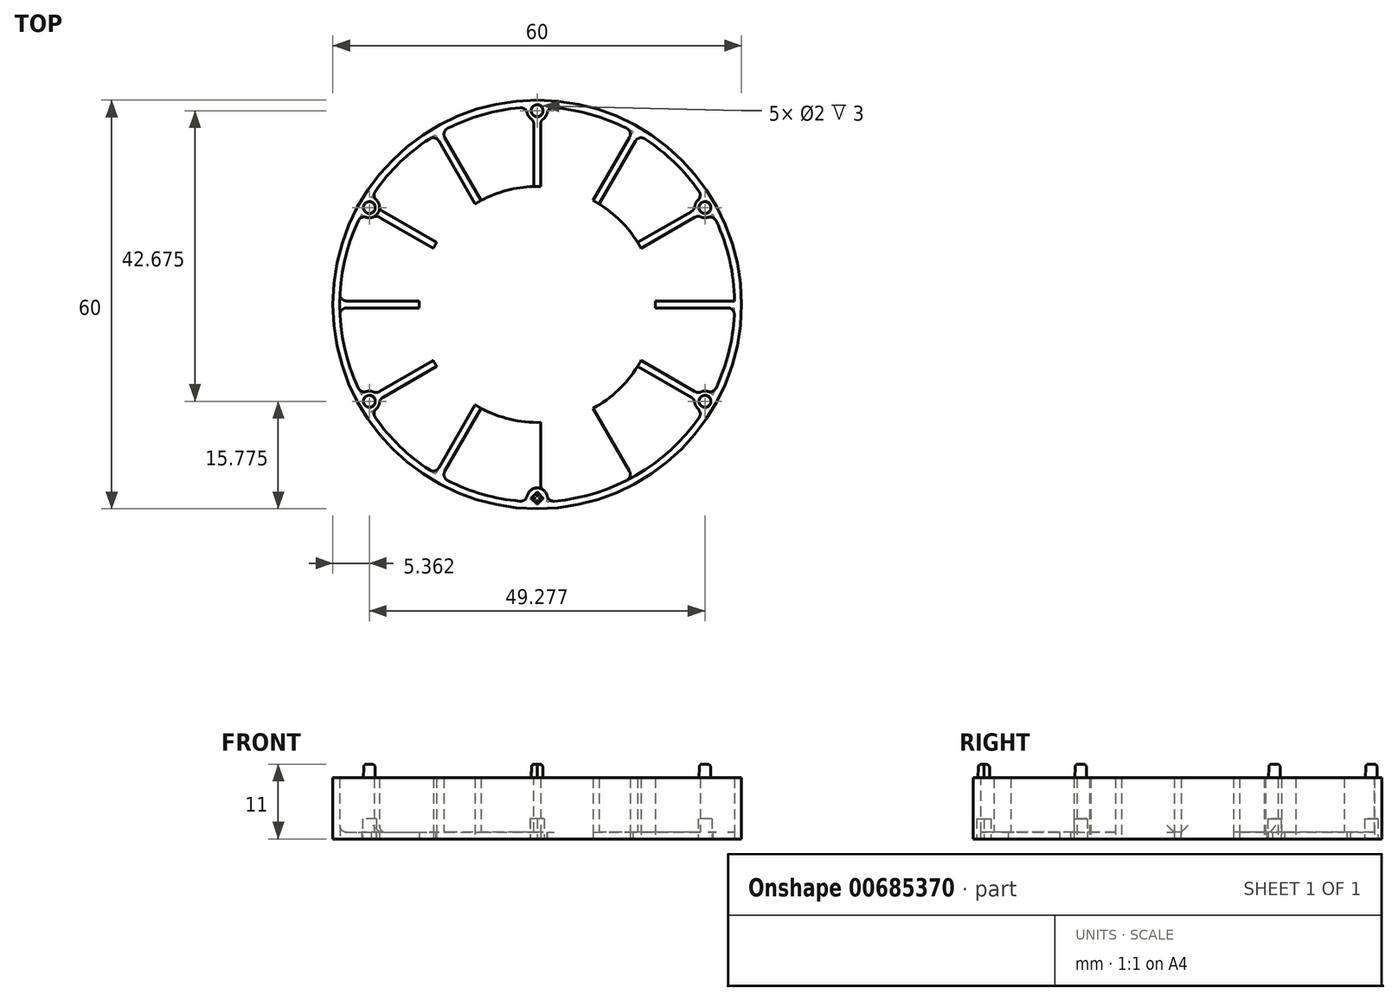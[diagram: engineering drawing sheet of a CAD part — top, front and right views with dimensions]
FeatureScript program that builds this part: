
annotation { "Feature Type Name" : "Feature", "Feature Type Description" : "" }
export const myFeature = defineFeature(function(context is Context, id is Id, definition is map)
    precondition{}
    {
        {
            var Q0;
            Q0=qCreatedBy(makeId("Top.planeOp"),FACE);
            var sketch = newSketch(context, id + "F0", { "sketchPlane" : qUnion([Q0])});
            skCircle(sketch, "E0", {"center": v(0, 0) * mm, "radius": 30 * mm});
            skCircle(sketch, "E1.0", {"center": v(0, 0) * mm, "radius": 29 * mm});
            skLineSegment(sketch, "E2.bottom", {"start": v(14.56, 26.23) * mm, "end": v(15.43, 25.73) * mm});
            skLineSegment(sketch, "E2.top", {"start": v(-15.43, -25.73) * mm, "end": v(-14.56, -26.23) * mm});
            skLineSegment(sketch, "E2.left", {"start": v(14.56, 26.23) * mm, "end": v(-15.43, -25.73) * mm});
            skLineSegment(sketch, "E2.right", {"start": v(15.43, 25.73) * mm, "end": v(-14.56, -26.23) * mm});
            skLineSegment(sketch, "E3.bottom", {"start": v(25.73, 15.43) * mm, "end": v(26.23, 14.56) * mm});
            skLineSegment(sketch, "E3.top", {"start": v(-26.23, -14.56) * mm, "end": v(-25.73, -15.43) * mm});
            skLineSegment(sketch, "E3.left", {"start": v(25.73, 15.43) * mm, "end": v(-26.23, -14.56) * mm});
            skLineSegment(sketch, "E3.right", {"start": v(26.23, 14.56) * mm, "end": v(-25.73, -15.43) * mm});
            skLineSegment(sketch, "E4", {"start": v(-38.35, 0) * mm, "end": v(39.17, 0) * mm, "construction": true});
            skLineSegment(sketch, "E5", {"start": v(0, 42.5) * mm, "end": v(0, -42.47) * mm, "construction": true});
            skLineSegment(sketch, "E6.bottom", {"start": v(-30, 0.5) * mm, "end": v(30, 0.5) * mm});
            skLineSegment(sketch, "E6.top", {"start": v(-30, -0.5) * mm, "end": v(30, -0.5) * mm});
            skLineSegment(sketch, "E6.left", {"start": v(-30, 0.5) * mm, "end": v(-30, -0.5) * mm});
            skLineSegment(sketch, "E6.right", {"start": v(30, 0.5) * mm, "end": v(30, -0.5) * mm});
            skLineSegment(sketch, "E7.bottom", {"start": v(-25.73, 15.43) * mm, "end": v(26.23, -14.56) * mm});
            skLineSegment(sketch, "E7.top", {"start": v(-26.23, 14.56) * mm, "end": v(25.73, -15.43) * mm});
            skLineSegment(sketch, "E7.left", {"start": v(-25.73, 15.43) * mm, "end": v(-26.23, 14.56) * mm});
            skLineSegment(sketch, "E7.right", {"start": v(26.23, -14.56) * mm, "end": v(25.73, -15.43) * mm});
            skLineSegment(sketch, "E8.bottom", {"start": v(-0.5, 30) * mm, "end": v(0.5, 30) * mm});
            skLineSegment(sketch, "E8.top", {"start": v(-0.5, -30) * mm, "end": v(0.5, -30) * mm});
            skLineSegment(sketch, "E8.left", {"start": v(-0.5, 30) * mm, "end": v(-0.5, -30) * mm});
            skLineSegment(sketch, "E8.right", {"start": v(0.5, 30) * mm, "end": v(0.5, -30) * mm});
            skLineSegment(sketch, "E9.bottom", {"start": v(-15.43, 25.73) * mm, "end": v(-14.56, 26.23) * mm});
            skLineSegment(sketch, "E9.top", {"start": v(14.56, -26.23) * mm, "end": v(15.43, -25.73) * mm});
            skLineSegment(sketch, "E9.left", {"start": v(-15.43, 25.73) * mm, "end": v(14.56, -26.23) * mm});
            skLineSegment(sketch, "E9.right", {"start": v(-14.56, 26.23) * mm, "end": v(15.43, -25.73) * mm});
            skCircle(sketch, "E10", {"center": v(0, 0) * mm, "radius": 17.33 * mm});
            skSolve(sketch);
        }
        {
            var Q0;
            Q0=qCreatedBy(makeId("Top.planeOp"),FACE);
            var sketch = newSketch(context, id + "F1", { "sketchPlane" : qUnion([Q0])});
            skCircle(sketch, "E11", {"center": v(0, 0) * mm, "radius": 30 * mm});
            skCircle(sketch, "E12", {"center": v(0, 0) * mm, "radius": 29 * mm});
            skSolve(sketch);
        }
        {
            var Q0;
            Q0=makeQuery(id+"F1.imprint","IMPRINT",FACE,{"disambiguationData":[TD([[makeQuery(id+"F1.imprint","IMPRINT",EDGE,{"derivedFrom":sQuery(id+"F1.wireOp",EDGE,"E11")}),1.0]])]});
            extrude(context, id + "F2", {"entities" : qUnion([Q0]), "depth" : 9 * mm, "offsetDistance" : 25 * mm});
        }
        {
            var Q0;
            {var subQ0=sQuery(id+"F0.wireOp",EDGE,"E2.right");var subQ1=sQuery(id+"F0.wireOp",EDGE,"E1.0");var subQ2=makeQuery(id+"F0.imprint","INTERSECT",VERTEX,{"disambiguationData":[OD(0.0)],"derivedFrom":[subQ1,subQ0]});Q0=makeQuery(id+"F0.imprint","IMPRINT",FACE,{"disambiguationData":[TD([[makeQuery(id+"F0.imprint","IMPRINT",EDGE,{"disambiguationData":[TD([[subQ2,-1.0]])],"derivedFrom":subQ1}),1.0]])]});}
            var Q1;
            {var subQ0=sQuery(id+"F0.wireOp",EDGE,"E6.bottom");var subQ1=sQuery(id+"F0.wireOp",EDGE,"E1.0");var subQ2=makeQuery(id+"F0.imprint","INTERSECT",VERTEX,{"disambiguationData":[OD(0.0)],"derivedFrom":[subQ1,subQ0]});Q1=makeQuery(id+"F0.imprint","IMPRINT",FACE,{"disambiguationData":[TD([[makeQuery(id+"F0.imprint","IMPRINT",EDGE,{"disambiguationData":[TD([[subQ2,1.0]])],"derivedFrom":subQ1}),1.0]])]});}
            var Q2;
            {var subQ0=sQuery(id+"F0.wireOp",EDGE,"E3.left");var subQ1=sQuery(id+"F0.wireOp",EDGE,"E1.0");var subQ2=makeQuery(id+"F0.imprint","INTERSECT",VERTEX,{"disambiguationData":[OD(1.0)],"derivedFrom":[subQ1,subQ0]});Q2=makeQuery(id+"F0.imprint","IMPRINT",FACE,{"disambiguationData":[TD([[makeQuery(id+"F0.imprint","IMPRINT",EDGE,{"disambiguationData":[TD([[subQ2,-1.0]])],"derivedFrom":subQ1}),1.0]])]});}
            var Q3;
            {var subQ0=sQuery(id+"F0.wireOp",EDGE,"E9.right");var subQ1=sQuery(id+"F0.wireOp",EDGE,"E1.0");var subQ2=makeQuery(id+"F0.imprint","INTERSECT",VERTEX,{"disambiguationData":[OD(0.0)],"derivedFrom":[subQ1,subQ0]});Q3=makeQuery(id+"F0.imprint","IMPRINT",FACE,{"disambiguationData":[TD([[makeQuery(id+"F0.imprint","IMPRINT",EDGE,{"disambiguationData":[TD([[subQ2,-1.0]])],"derivedFrom":subQ1}),1.0]])]});}
            var Q4;
            {var subQ0=sQuery(id+"F0.wireOp",EDGE,"E8.right");var subQ1=sQuery(id+"F0.wireOp",EDGE,"E1.0");var subQ2=makeQuery(id+"F0.imprint","INTERSECT",VERTEX,{"disambiguationData":[OD(0.0)],"derivedFrom":[subQ1,subQ0]});Q4=makeQuery(id+"F0.imprint","IMPRINT",FACE,{"disambiguationData":[TD([[makeQuery(id+"F0.imprint","IMPRINT",EDGE,{"disambiguationData":[TD([[subQ2,-1.0]])],"derivedFrom":subQ1}),1.0]])]});}
            var Q5;
            {var subQ0=sQuery(id+"F0.wireOp",EDGE,"E3.right");var subQ1=sQuery(id+"F0.wireOp",EDGE,"E1.0");var subQ2=makeQuery(id+"F0.imprint","INTERSECT",VERTEX,{"disambiguationData":[OD(0.0)],"derivedFrom":[subQ1,subQ0]});Q5=makeQuery(id+"F0.imprint","IMPRINT",FACE,{"disambiguationData":[TD([[makeQuery(id+"F0.imprint","IMPRINT",EDGE,{"disambiguationData":[TD([[subQ2,-1.0]])],"derivedFrom":subQ1}),1.0]])]});}
            var Q6;
            {var subQ0=sQuery(id+"F0.wireOp",EDGE,"E7.top");var subQ1=sQuery(id+"F0.wireOp",EDGE,"E1.0");var subQ2=makeQuery(id+"F0.imprint","INTERSECT",VERTEX,{"disambiguationData":[OD(1.0)],"derivedFrom":[subQ1,subQ0]});Q6=makeQuery(id+"F0.imprint","IMPRINT",FACE,{"disambiguationData":[TD([[makeQuery(id+"F0.imprint","IMPRINT",EDGE,{"disambiguationData":[TD([[subQ2,-1.0]])],"derivedFrom":subQ1}),1.0]])]});}
            var Q7;
            {var subQ0=sQuery(id+"F0.wireOp",EDGE,"E2.left");var subQ1=sQuery(id+"F0.wireOp",EDGE,"E1.0");var subQ2=makeQuery(id+"F0.imprint","INTERSECT",VERTEX,{"disambiguationData":[OD(1.0)],"derivedFrom":[subQ1,subQ0]});Q7=makeQuery(id+"F0.imprint","IMPRINT",FACE,{"disambiguationData":[TD([[makeQuery(id+"F0.imprint","IMPRINT",EDGE,{"disambiguationData":[TD([[subQ2,-1.0]])],"derivedFrom":subQ1}),1.0]])]});}
            extrude(context, id + "F3", {"entities" : qUnion([Q0, Q1, Q2, Q3, Q4, Q5, Q6, Q7]), "operationType" : NewBodyOperationType.ADD, "depth" : 9 * mm, "offsetDistance" : 25 * mm});
        }
        {
            var Q0;
            Q0=makeQuery(id+"F1.imprint","IMPRINT",FACE,{"disambiguationData":[TD([[makeQuery(id+"F1.imprint","IMPRINT",EDGE,{"derivedFrom":sQuery(id+"F1.wireOp",EDGE,"E11")}),1.0]])]});
            var Q1;
            Q1=makeQuery(id+"F1.imprint","IMPRINT",FACE,{"disambiguationData":[TD([[makeQuery(id+"F1.imprint","IMPRINT",EDGE,{"derivedFrom":sQuery(id+"F1.wireOp",EDGE,"E12")}),1.0]])]});
            extrude(context, id + "F4", {"entities" : qUnion([Q0, Q1]), "operationType" : NewBodyOperationType.ADD, "depth" : 1 * mm, "offsetDistance" : 25 * mm});
        }
        {
            var Q0;
            {var subQ0=sQuery(id+"F0.wireOp",EDGE,"E8.right");var subQ1=sQuery(id+"F0.wireOp",EDGE,"E1.0");var subQ2=makeQuery(id+"F0.imprint","INTERSECT",VERTEX,{"disambiguationData":[OD(1.0)],"derivedFrom":[subQ1,subQ0]});Q0=makeQuery(id+"F0.imprint","IMPRINT",FACE,{"disambiguationData":[TD([[makeQuery(id+"F0.imprint","IMPRINT",EDGE,{"disambiguationData":[TD([[subQ2,-1.0]])],"derivedFrom":subQ1}),1.0]])]});}
            var Q1;
            {var subQ0=sQuery(id+"F0.wireOp",EDGE,"E7.bottom");var subQ1=sQuery(id+"F0.wireOp",EDGE,"E1.0");var subQ2=makeQuery(id+"F0.imprint","INTERSECT",VERTEX,{"disambiguationData":[OD(1.0)],"derivedFrom":[subQ1,subQ0]});Q1=makeQuery(id+"F0.imprint","IMPRINT",FACE,{"disambiguationData":[TD([[makeQuery(id+"F0.imprint","IMPRINT",EDGE,{"disambiguationData":[TD([[subQ2,-1.0]])],"derivedFrom":subQ1}),1.0]])]});}
            var Q2;
            {var subQ0=sQuery(id+"F0.wireOp",EDGE,"E3.right");var subQ1=sQuery(id+"F0.wireOp",EDGE,"E1.0");var subQ2=makeQuery(id+"F0.imprint","INTERSECT",VERTEX,{"disambiguationData":[OD(0.0)],"derivedFrom":[subQ1,subQ0]});Q2=makeQuery(id+"F0.imprint","IMPRINT",FACE,{"disambiguationData":[TD([[makeQuery(id+"F0.imprint","IMPRINT",EDGE,{"disambiguationData":[TD([[subQ2,1.0]])],"derivedFrom":subQ1}),1.0]])]});}
            var Q3;
            {var subQ0=sQuery(id+"F0.wireOp",EDGE,"E2.left");var subQ1=sQuery(id+"F0.wireOp",EDGE,"E1.0");var subQ2=makeQuery(id+"F0.imprint","INTERSECT",VERTEX,{"disambiguationData":[OD(0.0)],"derivedFrom":[subQ1,subQ0]});Q3=makeQuery(id+"F0.imprint","IMPRINT",FACE,{"disambiguationData":[TD([[makeQuery(id+"F0.imprint","IMPRINT",EDGE,{"disambiguationData":[TD([[subQ2,-1.0]])],"derivedFrom":subQ1}),1.0]])]});}
            var Q4;
            {var subQ0=sQuery(id+"F0.wireOp",EDGE,"E9.left");var subQ1=sQuery(id+"F0.wireOp",EDGE,"E1.0");var subQ2=makeQuery(id+"F0.imprint","INTERSECT",VERTEX,{"disambiguationData":[OD(0.0)],"derivedFrom":[subQ1,subQ0]});Q4=makeQuery(id+"F0.imprint","IMPRINT",FACE,{"disambiguationData":[TD([[makeQuery(id+"F0.imprint","IMPRINT",EDGE,{"disambiguationData":[TD([[subQ2,-1.0]])],"derivedFrom":subQ1}),1.0]])]});}
            var Q5;
            {var subQ0=sQuery(id+"F0.wireOp",EDGE,"E7.top");var subQ1=sQuery(id+"F0.wireOp",EDGE,"E1.0");var subQ2=makeQuery(id+"F0.imprint","INTERSECT",VERTEX,{"disambiguationData":[OD(0.0)],"derivedFrom":[subQ1,subQ0]});Q5=makeQuery(id+"F0.imprint","IMPRINT",FACE,{"disambiguationData":[TD([[makeQuery(id+"F0.imprint","IMPRINT",EDGE,{"disambiguationData":[TD([[subQ2,-1.0]])],"derivedFrom":subQ1}),1.0]])]});}
            var Q6;
            {var subQ0=sQuery(id+"F0.wireOp",EDGE,"E6.top");var subQ1=sQuery(id+"F0.wireOp",EDGE,"E1.0");var subQ2=makeQuery(id+"F0.imprint","INTERSECT",VERTEX,{"disambiguationData":[OD(0.0)],"derivedFrom":[subQ1,subQ0]});Q6=makeQuery(id+"F0.imprint","IMPRINT",FACE,{"disambiguationData":[TD([[makeQuery(id+"F0.imprint","IMPRINT",EDGE,{"disambiguationData":[TD([[subQ2,-1.0]])],"derivedFrom":subQ1}),1.0]])]});}
            var Q7;
            {var subQ0=sQuery(id+"F0.wireOp",EDGE,"E3.right");var subQ1=sQuery(id+"F0.wireOp",EDGE,"E1.0");var subQ2=makeQuery(id+"F0.imprint","INTERSECT",VERTEX,{"disambiguationData":[OD(1.0)],"derivedFrom":[subQ1,subQ0]});Q7=makeQuery(id+"F0.imprint","IMPRINT",FACE,{"disambiguationData":[TD([[makeQuery(id+"F0.imprint","IMPRINT",EDGE,{"disambiguationData":[TD([[subQ2,-1.0]])],"derivedFrom":subQ1}),1.0]])]});}
            extrude(context, id + "F5", {"entities" : qUnion([Q0, Q1, Q2, Q3, Q4, Q5, Q6, Q7]), "operationType" : NewBodyOperationType.REMOVE, "depth" : 1 * mm, "offsetDistance" : 25 * mm});
        }
        {
            var Q0;
            Q0=qCreatedBy(makeId("Top.planeOp"),FACE);
            var sketch = newSketch(context, id + "F6", { "sketchPlane" : qUnion([Q0])});
            skCircle(sketch, "E13", {"center": v(0, 0) * mm, "radius": 28.45 * mm});
            skLineSegment(sketch, "E14", {"start": v(0, 28.45) * mm, "end": v(0, -28.45) * mm, "construction": true});
            skLineSegment(sketch, "E15", {"start": v(24.64, 14.22) * mm, "end": v(0, 0) * mm, "construction": true});
            skLineSegment(sketch, "E16", {"start": v(14.23, 24.64) * mm, "end": v(0, 0) * mm, "construction": true});
            skLineSegment(sketch, "E17", {"start": v(0, 0) * mm, "end": v(28.45, 0) * mm, "construction": true});
            skLineSegment(sketch, "E18", {"start": v(0, 0) * mm, "end": v(24.64, -14.22) * mm, "construction": true});
            skLineSegment(sketch, "E19", {"start": v(0, 0) * mm, "end": v(14.23, -24.64) * mm, "construction": true});
            skLineSegment(sketch, "E20", {"start": v(0, 0) * mm, "end": v(-14.23, 24.64) * mm, "construction": true});
            skLineSegment(sketch, "E21", {"start": v(0, 0) * mm, "end": v(-24.64, 14.22) * mm, "construction": true});
            skLineSegment(sketch, "E22", {"start": v(0, 0) * mm, "end": v(-28.45, 0) * mm, "construction": true});
            skLineSegment(sketch, "E23", {"start": v(0, 0) * mm, "end": v(-24.64, -14.23) * mm, "construction": true});
            skLineSegment(sketch, "E24", {"start": v(0, 0) * mm, "end": v(-14.22, -24.64) * mm, "construction": true});
            skCircle(sketch, "E25", {"center": v(0, 28.45) * mm, "radius": 1.5 * mm});
            skCircle(sketch, "E26", {"center": v(24.64, 14.22) * mm, "radius": 1.5 * mm});
            skCircle(sketch, "E27", {"center": v(24.64, -14.22) * mm, "radius": 1.5 * mm});
            skCircle(sketch, "E28", {"center": v(0, -28.45) * mm, "radius": 1.5 * mm});
            skCircle(sketch, "E29", {"center": v(-24.64, -14.23) * mm, "radius": 1.5 * mm});
            skCircle(sketch, "E30", {"center": v(-24.64, 14.22) * mm, "radius": 1.5 * mm});
            skCircle(sketch, "E31", {"center": v(-24.64, 14.22) * mm, "radius": 1 * mm});
            skCircle(sketch, "E32", {"center": v(0, 28.45) * mm, "radius": 1 * mm});
            skCircle(sketch, "E33", {"center": v(24.64, 14.22) * mm, "radius": 1 * mm});
            skCircle(sketch, "E34", {"center": v(24.64, -14.22) * mm, "radius": 1 * mm});
            skCircle(sketch, "E35", {"center": v(-24.64, -14.23) * mm, "radius": 1 * mm});
            skLineSegment(sketch, "E36.bottom", {"start": v(1.06, -28.45) * mm, "end": v(0, -29.51) * mm});
            skLineSegment(sketch, "E36.top", {"start": v(0, -27.39) * mm, "end": v(-1.06, -28.45) * mm});
            skLineSegment(sketch, "E36.left", {"start": v(1.06, -28.45) * mm, "end": v(0, -27.39) * mm});
            skLineSegment(sketch, "E36.right", {"start": v(0, -29.51) * mm, "end": v(-1.06, -28.45) * mm});
            skSolve(sketch);
        }
        {
            var Q0;
            {var subQ0=sQuery(id+"F6.wireOp",EDGE,"E30");var subQ1=sQuery(id+"F6.wireOp",EDGE,"E13");var subQ2=makeQuery(id+"F6.imprint","INTERSECT",VERTEX,{"disambiguationData":[OD(0.0)],"derivedFrom":[subQ1,subQ0]});Q0=makeQuery(id+"F6.imprint","IMPRINT",FACE,{"disambiguationData":[TD([[makeQuery(id+"F6.imprint","IMPRINT",EDGE,{"disambiguationData":[TD([[subQ2,-1.0]])],"derivedFrom":subQ1}),1.0]])]});}
            var Q1;
            {var subQ0=sQuery(id+"F6.wireOp",EDGE,"E30");var subQ1=sQuery(id+"F6.wireOp",EDGE,"E13");var subQ2=makeQuery(id+"F6.imprint","INTERSECT",VERTEX,{"disambiguationData":[OD(0.0)],"derivedFrom":[subQ1,subQ0]});Q1=makeQuery(id+"F6.imprint","IMPRINT",FACE,{"disambiguationData":[TD([[makeQuery(id+"F6.imprint","IMPRINT",EDGE,{"disambiguationData":[TD([[subQ2,-1.0]])],"derivedFrom":subQ1}),-1.0]])]});}
            var Q2;
            {var subQ0=sQuery(id+"F6.wireOp",EDGE,"E25");var subQ1=sQuery(id+"F6.wireOp",EDGE,"E13");var subQ2=makeQuery(id+"F6.imprint","INTERSECT",VERTEX,{"disambiguationData":[OD(0.0)],"derivedFrom":[subQ1,subQ0]});Q2=makeQuery(id+"F6.imprint","IMPRINT",FACE,{"disambiguationData":[TD([[makeQuery(id+"F6.imprint","IMPRINT",EDGE,{"disambiguationData":[TD([[subQ2,-1.0]])],"derivedFrom":subQ1}),1.0]])]});}
            var Q3;
            {var subQ0=sQuery(id+"F6.wireOp",EDGE,"E25");var subQ1=sQuery(id+"F6.wireOp",EDGE,"E13");var subQ2=makeQuery(id+"F6.imprint","INTERSECT",VERTEX,{"disambiguationData":[OD(0.0)],"derivedFrom":[subQ1,subQ0]});Q3=makeQuery(id+"F6.imprint","IMPRINT",FACE,{"disambiguationData":[TD([[makeQuery(id+"F6.imprint","IMPRINT",EDGE,{"disambiguationData":[TD([[subQ2,-1.0]])],"derivedFrom":subQ1}),-1.0]])]});}
            var Q4;
            {var subQ0=sQuery(id+"F6.wireOp",EDGE,"E26");var subQ1=sQuery(id+"F6.wireOp",EDGE,"E13");var subQ2=makeQuery(id+"F6.imprint","INTERSECT",VERTEX,{"disambiguationData":[OD(0.0)],"derivedFrom":[subQ1,subQ0]});Q4=makeQuery(id+"F6.imprint","IMPRINT",FACE,{"disambiguationData":[TD([[makeQuery(id+"F6.imprint","IMPRINT",EDGE,{"disambiguationData":[TD([[subQ2,-1.0]])],"derivedFrom":subQ1}),-1.0]])]});}
            var Q5;
            {var subQ0=sQuery(id+"F6.wireOp",EDGE,"E26");var subQ1=sQuery(id+"F6.wireOp",EDGE,"E13");var subQ2=makeQuery(id+"F6.imprint","INTERSECT",VERTEX,{"disambiguationData":[OD(0.0)],"derivedFrom":[subQ1,subQ0]});Q5=makeQuery(id+"F6.imprint","IMPRINT",FACE,{"disambiguationData":[TD([[makeQuery(id+"F6.imprint","IMPRINT",EDGE,{"disambiguationData":[TD([[subQ2,-1.0]])],"derivedFrom":subQ1}),1.0]])]});}
            var Q6;
            {var subQ0=sQuery(id+"F6.wireOp",EDGE,"E29");var subQ1=sQuery(id+"F6.wireOp",EDGE,"E13");var subQ2=makeQuery(id+"F6.imprint","INTERSECT",VERTEX,{"disambiguationData":[OD(0.0)],"derivedFrom":[subQ1,subQ0]});Q6=makeQuery(id+"F6.imprint","IMPRINT",FACE,{"disambiguationData":[TD([[makeQuery(id+"F6.imprint","IMPRINT",EDGE,{"disambiguationData":[TD([[subQ2,-1.0]])],"derivedFrom":subQ1}),1.0]])]});}
            var Q7;
            {var subQ0=sQuery(id+"F6.wireOp",EDGE,"E29");var subQ1=sQuery(id+"F6.wireOp",EDGE,"E13");var subQ2=makeQuery(id+"F6.imprint","INTERSECT",VERTEX,{"disambiguationData":[OD(0.0)],"derivedFrom":[subQ1,subQ0]});Q7=makeQuery(id+"F6.imprint","IMPRINT",FACE,{"disambiguationData":[TD([[makeQuery(id+"F6.imprint","IMPRINT",EDGE,{"disambiguationData":[TD([[subQ2,-1.0]])],"derivedFrom":subQ1}),-1.0]])]});}
            var Q8;
            {var subQ3=sQuery(id+"F6.wireOp",EDGE,"E13");var subQ5=sQuery(id+"F6.wireOp",EDGE,"E28");var subQ6=makeQuery(id+"F6.imprint","INTERSECT",VERTEX,{"disambiguationData":[OD(0.0)],"derivedFrom":[subQ3,subQ5]});Q8=makeQuery(id+"F6.imprint","IMPRINT",FACE,{"disambiguationData":[TD([[makeQuery(id+"F6.imprint","IMPRINT",EDGE,{"disambiguationData":[TD([[subQ6,-1.0]])],"derivedFrom":subQ3}),1.0]])]});}
            var Q9;
            {var subQ6=sQuery(id+"F6.wireOp",EDGE,"E36.bottom");Q9=makeQuery(id+"F6.imprint","IMPRINT",FACE,{"disambiguationData":[TD([[makeQuery(id+"F6.imprint","IMPRINT",EDGE,{"derivedFrom":subQ6}),1.0]])]});}
            var Q10;
            {var subQ0=sQuery(id+"F6.wireOp",EDGE,"E27");var subQ1=sQuery(id+"F6.wireOp",EDGE,"E13");var subQ2=makeQuery(id+"F6.imprint","INTERSECT",VERTEX,{"disambiguationData":[OD(0.0)],"derivedFrom":[subQ1,subQ0]});Q10=makeQuery(id+"F6.imprint","IMPRINT",FACE,{"disambiguationData":[TD([[makeQuery(id+"F6.imprint","IMPRINT",EDGE,{"disambiguationData":[TD([[subQ2,-1.0]])],"derivedFrom":subQ1}),-1.0]])]});}
            var Q11;
            {var subQ0=sQuery(id+"F6.wireOp",EDGE,"E27");var subQ1=sQuery(id+"F6.wireOp",EDGE,"E13");var subQ2=makeQuery(id+"F6.imprint","INTERSECT",VERTEX,{"disambiguationData":[OD(0.0)],"derivedFrom":[subQ1,subQ0]});Q11=makeQuery(id+"F6.imprint","IMPRINT",FACE,{"disambiguationData":[TD([[makeQuery(id+"F6.imprint","IMPRINT",EDGE,{"disambiguationData":[TD([[subQ2,-1.0]])],"derivedFrom":subQ1}),1.0]])]});}
            var Q12;
            {var subQ0=sQuery(id+"F6.wireOp",EDGE,"E31");var subQ1=sQuery(id+"F6.wireOp",EDGE,"E13");var subQ2=makeQuery(id+"F6.imprint","INTERSECT",VERTEX,{"disambiguationData":[OD(0.0)],"derivedFrom":[subQ1,subQ0]});Q12=makeQuery(id+"F6.imprint","IMPRINT",FACE,{"disambiguationData":[TD([[makeQuery(id+"F6.imprint","IMPRINT",EDGE,{"disambiguationData":[TD([[subQ2,-1.0]])],"derivedFrom":subQ1}),1.0]])]});}
            var Q13;
            {var subQ0=sQuery(id+"F6.wireOp",EDGE,"E31");var subQ1=sQuery(id+"F6.wireOp",EDGE,"E13");var subQ2=makeQuery(id+"F6.imprint","INTERSECT",VERTEX,{"disambiguationData":[OD(0.0)],"derivedFrom":[subQ1,subQ0]});Q13=makeQuery(id+"F6.imprint","IMPRINT",FACE,{"disambiguationData":[TD([[makeQuery(id+"F6.imprint","IMPRINT",EDGE,{"disambiguationData":[TD([[subQ2,-1.0]])],"derivedFrom":subQ1}),-1.0]])]});}
            var Q14;
            {var subQ0=sQuery(id+"F6.wireOp",EDGE,"E32");var subQ1=sQuery(id+"F6.wireOp",EDGE,"E13");var subQ2=makeQuery(id+"F6.imprint","INTERSECT",VERTEX,{"disambiguationData":[OD(0.0)],"derivedFrom":[subQ1,subQ0]});Q14=makeQuery(id+"F6.imprint","IMPRINT",FACE,{"disambiguationData":[TD([[makeQuery(id+"F6.imprint","IMPRINT",EDGE,{"disambiguationData":[TD([[subQ2,-1.0]])],"derivedFrom":subQ1}),-1.0]])]});}
            var Q15;
            {var subQ0=sQuery(id+"F6.wireOp",EDGE,"E32");var subQ1=sQuery(id+"F6.wireOp",EDGE,"E13");var subQ2=makeQuery(id+"F6.imprint","INTERSECT",VERTEX,{"disambiguationData":[OD(0.0)],"derivedFrom":[subQ1,subQ0]});Q15=makeQuery(id+"F6.imprint","IMPRINT",FACE,{"disambiguationData":[TD([[makeQuery(id+"F6.imprint","IMPRINT",EDGE,{"disambiguationData":[TD([[subQ2,-1.0]])],"derivedFrom":subQ1}),1.0]])]});}
            var Q16;
            {var subQ0=sQuery(id+"F6.wireOp",EDGE,"E33");var subQ1=sQuery(id+"F6.wireOp",EDGE,"E13");var subQ2=makeQuery(id+"F6.imprint","INTERSECT",VERTEX,{"disambiguationData":[OD(0.0)],"derivedFrom":[subQ1,subQ0]});Q16=makeQuery(id+"F6.imprint","IMPRINT",FACE,{"disambiguationData":[TD([[makeQuery(id+"F6.imprint","IMPRINT",EDGE,{"disambiguationData":[TD([[subQ2,-1.0]])],"derivedFrom":subQ1}),-1.0]])]});}
            var Q17;
            {var subQ0=sQuery(id+"F6.wireOp",EDGE,"E33");var subQ1=sQuery(id+"F6.wireOp",EDGE,"E13");var subQ2=makeQuery(id+"F6.imprint","INTERSECT",VERTEX,{"disambiguationData":[OD(0.0)],"derivedFrom":[subQ1,subQ0]});Q17=makeQuery(id+"F6.imprint","IMPRINT",FACE,{"disambiguationData":[TD([[makeQuery(id+"F6.imprint","IMPRINT",EDGE,{"disambiguationData":[TD([[subQ2,-1.0]])],"derivedFrom":subQ1}),1.0]])]});}
            var Q18;
            {var subQ0=sQuery(id+"F6.wireOp",EDGE,"E34");var subQ1=sQuery(id+"F6.wireOp",EDGE,"E13");var subQ2=makeQuery(id+"F6.imprint","INTERSECT",VERTEX,{"disambiguationData":[OD(0.0)],"derivedFrom":[subQ1,subQ0]});Q18=makeQuery(id+"F6.imprint","IMPRINT",FACE,{"disambiguationData":[TD([[makeQuery(id+"F6.imprint","IMPRINT",EDGE,{"disambiguationData":[TD([[subQ2,-1.0]])],"derivedFrom":subQ1}),-1.0]])]});}
            var Q19;
            {var subQ0=sQuery(id+"F6.wireOp",EDGE,"E34");var subQ1=sQuery(id+"F6.wireOp",EDGE,"E13");var subQ2=makeQuery(id+"F6.imprint","INTERSECT",VERTEX,{"disambiguationData":[OD(0.0)],"derivedFrom":[subQ1,subQ0]});Q19=makeQuery(id+"F6.imprint","IMPRINT",FACE,{"disambiguationData":[TD([[makeQuery(id+"F6.imprint","IMPRINT",EDGE,{"disambiguationData":[TD([[subQ2,-1.0]])],"derivedFrom":subQ1}),1.0]])]});}
            var Q20;
            {var subQ1=sQuery(id+"F6.wireOp",EDGE,"E36.bottom");Q20=makeQuery(id+"F6.imprint","IMPRINT",FACE,{"disambiguationData":[TD([[makeQuery(id+"F6.imprint","IMPRINT",EDGE,{"derivedFrom":subQ1}),-1.0]])]});}
            var Q21;
            {var subQ0=sQuery(id+"F6.wireOp",EDGE,"E35");var subQ1=sQuery(id+"F6.wireOp",EDGE,"E13");var subQ2=makeQuery(id+"F6.imprint","INTERSECT",VERTEX,{"disambiguationData":[OD(0.0)],"derivedFrom":[subQ1,subQ0]});Q21=makeQuery(id+"F6.imprint","IMPRINT",FACE,{"disambiguationData":[TD([[makeQuery(id+"F6.imprint","IMPRINT",EDGE,{"disambiguationData":[TD([[subQ2,-1.0]])],"derivedFrom":subQ1}),-1.0]])]});}
            var Q22;
            {var subQ0=sQuery(id+"F6.wireOp",EDGE,"E35");var subQ1=sQuery(id+"F6.wireOp",EDGE,"E13");var subQ2=makeQuery(id+"F6.imprint","INTERSECT",VERTEX,{"disambiguationData":[OD(0.0)],"derivedFrom":[subQ1,subQ0]});Q22=makeQuery(id+"F6.imprint","IMPRINT",FACE,{"disambiguationData":[TD([[makeQuery(id+"F6.imprint","IMPRINT",EDGE,{"disambiguationData":[TD([[subQ2,-1.0]])],"derivedFrom":subQ1}),1.0]])]});}
            var Q23;
            {var subQ0=sQuery(id+"F6.wireOp",EDGE,"E36.top");var subQ1=sQuery(id+"F6.wireOp",EDGE,"E13");var subQ2=makeQuery(id+"F6.imprint","INTERSECT",VERTEX,{"derivedFrom":[subQ1,subQ0]});Q23=makeQuery(id+"F6.imprint","IMPRINT",FACE,{"disambiguationData":[TD([[makeQuery(id+"F6.imprint","IMPRINT",EDGE,{"disambiguationData":[TD([[subQ2,-1.0]])],"derivedFrom":subQ1}),1.0]])]});}
            extrude(context, id + "F7", {"entities" : qUnion([Q0, Q1, Q2, Q3, Q4, Q5, Q6, Q7, Q8, Q9, Q10, Q11, Q12, Q13, Q14, Q15, Q16, Q17, Q18, Q19, Q20, Q21, Q22, Q23]), "operationType" : NewBodyOperationType.ADD, "depth" : 9 * mm, "offsetDistance" : 25 * mm});
        }
        {
            var Q0;
            {var subQ0=sQuery(id+"F0.wireOp",EDGE,"E8.right");var subQ1=sQuery(id+"F0.wireOp",EDGE,"E1.0");Q0=makeQuery(id+"F3.opExtrude","SWEPT_EDGE",EDGE,{"disambiguationData":[OSD([subQ1,subQ0]),TDD([makeQuery(id+"F0.imprint","INTERSECT",VERTEX,{"disambiguationData":[OD(1.0)],"derivedFrom":[subQ1,subQ0]})])]});}
            var Q1;
            {var subQ0=sQuery(id+"F0.wireOp",EDGE,"E2.left");var subQ1=sQuery(id+"F0.wireOp",EDGE,"E1.0");Q1=makeQuery(id+"F3.opExtrude","SWEPT_EDGE",EDGE,{"disambiguationData":[OSD([subQ1,subQ0]),TDD([makeQuery(id+"F0.imprint","INTERSECT",VERTEX,{"disambiguationData":[OD(1.0)],"derivedFrom":[subQ1,subQ0]})])]});}
            var Q2;
            {var subQ0=sQuery(id+"F0.wireOp",EDGE,"E3.left");var subQ1=sQuery(id+"F0.wireOp",EDGE,"E1.0");Q2=makeQuery(id+"F3.opExtrude","SWEPT_EDGE",EDGE,{"disambiguationData":[OSD([subQ1,subQ0]),TDD([makeQuery(id+"F0.imprint","INTERSECT",VERTEX,{"disambiguationData":[OD(1.0)],"derivedFrom":[subQ1,subQ0]})])]});}
            var Q3;
            {var subQ0=sQuery(id+"F0.wireOp",EDGE,"E6.bottom");var subQ1=sQuery(id+"F0.wireOp",EDGE,"E1.0");Q3=makeQuery(id+"F3.opExtrude","SWEPT_EDGE",EDGE,{"disambiguationData":[OSD([subQ1,subQ0]),TDD([makeQuery(id+"F0.imprint","INTERSECT",VERTEX,{"disambiguationData":[OD(1.0)],"derivedFrom":[subQ1,subQ0]})])]});}
            var Q4;
            {var subQ0=sQuery(id+"F0.wireOp",EDGE,"E9.right");var subQ1=sQuery(id+"F0.wireOp",EDGE,"E1.0");Q4=makeQuery(id+"F3.opExtrude","SWEPT_EDGE",EDGE,{"disambiguationData":[OSD([subQ1,subQ0]),TDD([makeQuery(id+"F0.imprint","INTERSECT",VERTEX,{"disambiguationData":[OD(1.0)],"derivedFrom":[subQ1,subQ0]})])]});}
            var Q5;
            {var subQ0=sQuery(id+"F0.wireOp",EDGE,"E7.bottom");var subQ1=sQuery(id+"F0.wireOp",EDGE,"E1.0");Q5=makeQuery(id+"F3.opExtrude","SWEPT_EDGE",EDGE,{"disambiguationData":[OSD([subQ1,subQ0]),TDD([makeQuery(id+"F0.imprint","INTERSECT",VERTEX,{"disambiguationData":[OD(1.0)],"derivedFrom":[subQ1,subQ0]})])]});}
            var Q6;
            {var subQ0=sQuery(id+"F0.wireOp",EDGE,"E8.left");var subQ1=sQuery(id+"F0.wireOp",EDGE,"E1.0");Q6=makeQuery(id+"F3.opExtrude","SWEPT_EDGE",EDGE,{"disambiguationData":[OSD([subQ1,subQ0]),TDD([makeQuery(id+"F0.imprint","INTERSECT",VERTEX,{"disambiguationData":[OD(0.0)],"derivedFrom":[subQ1,subQ0]})])]});}
            var Q7;
            {var subQ0=sQuery(id+"F0.wireOp",EDGE,"E2.left");var subQ1=sQuery(id+"F0.wireOp",EDGE,"E1.0");Q7=makeQuery(id+"F3.opExtrude","SWEPT_EDGE",EDGE,{"disambiguationData":[OSD([subQ1,subQ0]),TDD([makeQuery(id+"F0.imprint","INTERSECT",VERTEX,{"disambiguationData":[OD(0.0)],"derivedFrom":[subQ1,subQ0]})])]});}
            var Q8;
            {var subQ0=sQuery(id+"F0.wireOp",EDGE,"E3.left");var subQ1=sQuery(id+"F0.wireOp",EDGE,"E1.0");Q8=makeQuery(id+"F3.opExtrude","SWEPT_EDGE",EDGE,{"disambiguationData":[OSD([subQ1,subQ0]),TDD([makeQuery(id+"F0.imprint","INTERSECT",VERTEX,{"disambiguationData":[OD(0.0)],"derivedFrom":[subQ1,subQ0]})])]});}
            var Q9;
            {var subQ0=sQuery(id+"F0.wireOp",EDGE,"E6.top");var subQ1=sQuery(id+"F0.wireOp",EDGE,"E1.0");Q9=makeQuery(id+"F3.opExtrude","SWEPT_EDGE",EDGE,{"disambiguationData":[OSD([subQ1,subQ0]),TDD([makeQuery(id+"F0.imprint","INTERSECT",VERTEX,{"disambiguationData":[OD(1.0)],"derivedFrom":[subQ1,subQ0]})])]});}
            var Q10;
            {var subQ0=sQuery(id+"F0.wireOp",EDGE,"E7.top");var subQ1=sQuery(id+"F0.wireOp",EDGE,"E1.0");Q10=makeQuery(id+"F3.opExtrude","SWEPT_EDGE",EDGE,{"disambiguationData":[OSD([subQ1,subQ0]),TDD([makeQuery(id+"F0.imprint","INTERSECT",VERTEX,{"disambiguationData":[OD(0.0)],"derivedFrom":[subQ1,subQ0]})])]});}
            var Q11;
            {var subQ0=sQuery(id+"F0.wireOp",EDGE,"E6.top");var subQ1=sQuery(id+"F0.wireOp",EDGE,"E1.0");Q11=makeQuery(id+"F3.opExtrude","SWEPT_EDGE",EDGE,{"disambiguationData":[OSD([subQ1,subQ0]),TDD([makeQuery(id+"F0.imprint","INTERSECT",VERTEX,{"disambiguationData":[OD(0.0)],"derivedFrom":[subQ1,subQ0]})])]});}
            var Q12;
            {var subQ0=sQuery(id+"F0.wireOp",EDGE,"E9.left");var subQ1=sQuery(id+"F0.wireOp",EDGE,"E1.0");Q12=makeQuery(id+"F3.opExtrude","SWEPT_EDGE",EDGE,{"disambiguationData":[OSD([subQ1,subQ0]),TDD([makeQuery(id+"F0.imprint","INTERSECT",VERTEX,{"disambiguationData":[OD(0.0)],"derivedFrom":[subQ1,subQ0]})])]});}
            var Q13;
            {var subQ0=sQuery(id+"F0.wireOp",EDGE,"E8.right");var subQ1=sQuery(id+"F0.wireOp",EDGE,"E1.0");Q13=makeQuery(id+"F3.opExtrude","SWEPT_EDGE",EDGE,{"disambiguationData":[OSD([subQ1,subQ0]),TDD([makeQuery(id+"F0.imprint","INTERSECT",VERTEX,{"disambiguationData":[OD(0.0)],"derivedFrom":[subQ1,subQ0]})])]});}
            var Q14;
            {var subQ0=sQuery(id+"F0.wireOp",EDGE,"E7.bottom");var subQ1=sQuery(id+"F0.wireOp",EDGE,"E1.0");Q14=makeQuery(id+"F3.opExtrude","SWEPT_EDGE",EDGE,{"disambiguationData":[OSD([subQ1,subQ0]),TDD([makeQuery(id+"F0.imprint","INTERSECT",VERTEX,{"disambiguationData":[OD(0.0)],"derivedFrom":[subQ1,subQ0]})])]});}
            var Q15;
            {var subQ0=sQuery(id+"F0.wireOp",EDGE,"E9.right");var subQ1=sQuery(id+"F0.wireOp",EDGE,"E1.0");Q15=makeQuery(id+"F3.opExtrude","SWEPT_EDGE",EDGE,{"disambiguationData":[OSD([subQ1,subQ0]),TDD([makeQuery(id+"F0.imprint","INTERSECT",VERTEX,{"disambiguationData":[OD(0.0)],"derivedFrom":[subQ1,subQ0]})])]});}
            var Q16;
            {var subQ0=sQuery(id+"F0.wireOp",EDGE,"E3.right");var subQ1=sQuery(id+"F0.wireOp",EDGE,"E1.0");Q16=makeQuery(id+"F3.opExtrude","SWEPT_EDGE",EDGE,{"disambiguationData":[OSD([subQ1,subQ0]),TDD([makeQuery(id+"F0.imprint","INTERSECT",VERTEX,{"disambiguationData":[OD(1.0)],"derivedFrom":[subQ1,subQ0]})])]});}
            var Q17;
            {var subQ0=sQuery(id+"F0.wireOp",EDGE,"E2.right");var subQ1=sQuery(id+"F0.wireOp",EDGE,"E1.0");Q17=makeQuery(id+"F3.opExtrude","SWEPT_EDGE",EDGE,{"disambiguationData":[OSD([subQ1,subQ0]),TDD([makeQuery(id+"F0.imprint","INTERSECT",VERTEX,{"disambiguationData":[OD(1.0)],"derivedFrom":[subQ1,subQ0]})])]});}
            var Q18;
            {var subQ0=sQuery(id+"F0.wireOp",EDGE,"E3.right");var subQ1=sQuery(id+"F0.wireOp",EDGE,"E1.0");Q18=makeQuery(id+"F3.opExtrude","SWEPT_EDGE",EDGE,{"disambiguationData":[OSD([subQ1,subQ0]),TDD([makeQuery(id+"F0.imprint","INTERSECT",VERTEX,{"disambiguationData":[OD(0.0)],"derivedFrom":[subQ1,subQ0]})])]});}
            var Q19;
            {var subQ0=sQuery(id+"F0.wireOp",EDGE,"E2.right");var subQ1=sQuery(id+"F0.wireOp",EDGE,"E1.0");Q19=makeQuery(id+"F3.opExtrude","SWEPT_EDGE",EDGE,{"disambiguationData":[OSD([subQ1,subQ0]),TDD([makeQuery(id+"F0.imprint","INTERSECT",VERTEX,{"disambiguationData":[OD(0.0)],"derivedFrom":[subQ1,subQ0]})])]});}
            var Q20;
            {var subQ0=sQuery(id+"F0.wireOp",EDGE,"E8.left");var subQ1=sQuery(id+"F0.wireOp",EDGE,"E1.0");Q20=makeQuery(id+"F3.opExtrude","SWEPT_EDGE",EDGE,{"disambiguationData":[OSD([subQ1,subQ0]),TDD([makeQuery(id+"F0.imprint","INTERSECT",VERTEX,{"disambiguationData":[OD(1.0)],"derivedFrom":[subQ1,subQ0]})])]});}
            var Q21;
            {var subQ0=sQuery(id+"F0.wireOp",EDGE,"E9.left");var subQ1=sQuery(id+"F0.wireOp",EDGE,"E1.0");Q21=makeQuery(id+"F3.opExtrude","SWEPT_EDGE",EDGE,{"disambiguationData":[OSD([subQ1,subQ0]),TDD([makeQuery(id+"F0.imprint","INTERSECT",VERTEX,{"disambiguationData":[OD(1.0)],"derivedFrom":[subQ1,subQ0]})])]});}
            var Q22;
            {var subQ0=sQuery(id+"F0.wireOp",EDGE,"E7.top");var subQ1=sQuery(id+"F0.wireOp",EDGE,"E1.0");Q22=makeQuery(id+"F3.opExtrude","SWEPT_EDGE",EDGE,{"disambiguationData":[OSD([subQ1,subQ0]),TDD([makeQuery(id+"F0.imprint","INTERSECT",VERTEX,{"disambiguationData":[OD(1.0)],"derivedFrom":[subQ1,subQ0]})])]});}
            var Q23;
            {var subQ0=sQuery(id+"F0.wireOp",EDGE,"E6.bottom");var subQ1=sQuery(id+"F0.wireOp",EDGE,"E1.0");Q23=makeQuery(id+"F3.opExtrude","SWEPT_EDGE",EDGE,{"disambiguationData":[OSD([subQ1,subQ0]),TDD([makeQuery(id+"F0.imprint","INTERSECT",VERTEX,{"disambiguationData":[OD(0.0)],"derivedFrom":[subQ1,subQ0]})])]});}
            var Q24;
            {var subQ0=sQuery(id+"F0.wireOp",EDGE,"E8.right");var subQ1=sQuery(id+"F0.wireOp",EDGE,"E1.0");var subQ19=sQuery(id+"F1.wireOp",EDGE,"E12");var subQ44=sQuery(id+"F0.wireOp",EDGE,"E7.top");Q24=makeQuery(id+"F7.boolean.opBoolean","INTERSECT",EDGE,{"disambiguationData":[OD(0.0)],"derivedFrom":[makeQuery(id+"F5.boolean.opBoolean","MERGE",FACE,{"derivedFrom":[makeQuery(id+"F3.boolean.opBoolean","SPLIT",FACE,{"disambiguationData":[TD([makeQuery(id+"F3.opExtrude","SWEPT_FACE",FACE,{"disambiguationData":[OSD([subQ44])]})])],"derivedFrom":makeQuery(id+"F2.opExtrude","SWEPT_FACE",FACE,{"disambiguationData":[OSD([subQ19])]})}),makeQuery(id+"F5.opExtrude","SWEPT_FACE",FACE,{"disambiguationData":[OSD([subQ1]),TDD([makeQuery(id+"F0.imprint","IMPRINT",EDGE,{"disambiguationData":[TD([[makeQuery(id+"F0.imprint","INTERSECT",VERTEX,{"disambiguationData":[OD(1.0)],"derivedFrom":[subQ1,subQ0]}),-1.0]])],"derivedFrom":subQ1})])]})]}),makeQuery(id+"F7.opExtrude","SWEPT_FACE",FACE,{"disambiguationData":[OSD([sQuery(id+"F6.wireOp",EDGE,"E28")])]})]});}
            var Q25;
            {var subQ0=sQuery(id+"F0.wireOp",EDGE,"E8.right");Q25=makeQuery(id+"F7.boolean.opBoolean","INTERSECT",EDGE,{"derivedFrom":[makeQuery(id+"F5.boolean.opBoolean","COPY",FACE,{"derivedFrom":makeQuery(id+"F5.opExtrude","SWEPT_FACE",FACE,{"disambiguationData":[OSD([subQ0]),TDD([makeQuery(id+"F0.imprint","IMPRINT",EDGE,{"disambiguationData":[TD([[makeQuery(id+"F0.imprint","INTERSECT",VERTEX,{"disambiguationData":[OD(1.0)],"derivedFrom":[sQuery(id+"F0.wireOp",EDGE,"E1.0"),subQ0]}),1.0]])],"derivedFrom":subQ0})])]})}),makeQuery(id+"F7.opExtrude","SWEPT_FACE",FACE,{"disambiguationData":[OSD([sQuery(id+"F6.wireOp",EDGE,"E28")])]})]});}
            var Q26;
            {var subQ0=sQuery(id+"F0.wireOp",EDGE,"E7.bottom");Q26=makeQuery(id+"F7.boolean.opBoolean","INTERSECT",EDGE,{"derivedFrom":[makeQuery(id+"F5.boolean.opBoolean","MERGE",FACE,{"derivedFrom":[makeQuery(id+"F3.opExtrude","SWEPT_FACE",FACE,{"disambiguationData":[OSD([subQ0])]}),makeQuery(id+"F5.opExtrude","SWEPT_FACE",FACE,{"disambiguationData":[OSD([subQ0]),TDD([makeQuery(id+"F0.imprint","IMPRINT",EDGE,{"disambiguationData":[TD([[makeQuery(id+"F0.imprint","INTERSECT",VERTEX,{"disambiguationData":[OD(1.0)],"derivedFrom":[sQuery(id+"F0.wireOp",EDGE,"E1.0"),subQ0]}),1.0]])],"derivedFrom":subQ0})])]})]}),makeQuery(id+"F7.opExtrude","SWEPT_FACE",FACE,{"disambiguationData":[OSD([sQuery(id+"F6.wireOp",EDGE,"E27")])]})]});}
            var Q27;
            {var subQ0=sQuery(id+"F0.wireOp",EDGE,"E7.bottom");var subQ1=sQuery(id+"F0.wireOp",EDGE,"E1.0");var subQ2=sQuery(id+"F0.wireOp",EDGE,"E6.top");var subQ18=sQuery(id+"F1.wireOp",EDGE,"E12");Q27=makeQuery(id+"F7.boolean.opBoolean","INTERSECT",EDGE,{"derivedFrom":[makeQuery(id+"F5.boolean.opBoolean","MERGE",FACE,{"derivedFrom":[makeQuery(id+"F3.boolean.opBoolean","SPLIT",FACE,{"disambiguationData":[TD([makeQuery(id+"F3.opExtrude","SWEPT_FACE",FACE,{"disambiguationData":[OSD([subQ2])]})])],"derivedFrom":makeQuery(id+"F2.opExtrude","SWEPT_FACE",FACE,{"disambiguationData":[OSD([subQ18])]})}),makeQuery(id+"F5.opExtrude","SWEPT_FACE",FACE,{"disambiguationData":[OSD([subQ1]),TDD([makeQuery(id+"F0.imprint","IMPRINT",EDGE,{"disambiguationData":[TD([[makeQuery(id+"F0.imprint","INTERSECT",VERTEX,{"disambiguationData":[OD(1.0)],"derivedFrom":[subQ1,subQ0]}),-1.0]])],"derivedFrom":subQ1})])]})]}),makeQuery(id+"F7.opExtrude","SWEPT_FACE",FACE,{"disambiguationData":[OSD([sQuery(id+"F6.wireOp",EDGE,"E27")])]})]});}
            var Q28;
            {var subQ0=sQuery(id+"F0.wireOp",EDGE,"E9.left");var subQ1=sQuery(id+"F0.wireOp",EDGE,"E1.0");Q28=makeQuery(id+"F5.boolean.opBoolean","COPY",EDGE,{"derivedFrom":makeQuery(id+"F5.opExtrude","SWEPT_EDGE",EDGE,{"disambiguationData":[OSD([subQ1,subQ0]),TDD([makeQuery(id+"F0.imprint","INTERSECT",VERTEX,{"disambiguationData":[OD(1.0)],"derivedFrom":[subQ1,subQ0]})])]})});}
            var Q29;
            {var subQ0=sQuery(id+"F0.wireOp",EDGE,"E8.right");var subQ1=sQuery(id+"F0.wireOp",EDGE,"E1.0");var subQ19=sQuery(id+"F1.wireOp",EDGE,"E12");var subQ44=sQuery(id+"F0.wireOp",EDGE,"E7.top");Q29=makeQuery(id+"F7.boolean.opBoolean","INTERSECT",EDGE,{"disambiguationData":[OD(1.0)],"derivedFrom":[makeQuery(id+"F5.boolean.opBoolean","MERGE",FACE,{"derivedFrom":[makeQuery(id+"F3.boolean.opBoolean","SPLIT",FACE,{"disambiguationData":[TD([makeQuery(id+"F3.opExtrude","SWEPT_FACE",FACE,{"disambiguationData":[OSD([subQ44])]})])],"derivedFrom":makeQuery(id+"F2.opExtrude","SWEPT_FACE",FACE,{"disambiguationData":[OSD([subQ19])]})}),makeQuery(id+"F5.opExtrude","SWEPT_FACE",FACE,{"disambiguationData":[OSD([subQ1]),TDD([makeQuery(id+"F0.imprint","IMPRINT",EDGE,{"disambiguationData":[TD([[makeQuery(id+"F0.imprint","INTERSECT",VERTEX,{"disambiguationData":[OD(1.0)],"derivedFrom":[subQ1,subQ0]}),-1.0]])],"derivedFrom":subQ1})])]})]}),makeQuery(id+"F7.opExtrude","SWEPT_FACE",FACE,{"disambiguationData":[OSD([sQuery(id+"F6.wireOp",EDGE,"E28")])]})]});}
            var Q30;
            {var subQ0=sQuery(id+"F0.wireOp",EDGE,"E3.left");Q30=makeQuery(id+"F7.boolean.opBoolean","INTERSECT",EDGE,{"derivedFrom":[makeQuery(id+"F5.boolean.opBoolean","MERGE",FACE,{"derivedFrom":[makeQuery(id+"F3.opExtrude","SWEPT_FACE",FACE,{"disambiguationData":[OSD([subQ0]),TDD([makeQuery(id+"F0.imprint","IMPRINT",EDGE,{"disambiguationData":[TD([[makeQuery(id+"F0.imprint","INTERSECT",VERTEX,{"disambiguationData":[OD(1.0)],"derivedFrom":[sQuery(id+"F0.wireOp",EDGE,"E1.0"),subQ0]}),1.0]])],"derivedFrom":subQ0})])]}),makeQuery(id+"F5.opExtrude","SWEPT_FACE",FACE,{"disambiguationData":[OSD([subQ0])]})]}),makeQuery(id+"F7.opExtrude","SWEPT_FACE",FACE,{"disambiguationData":[OSD([sQuery(id+"F6.wireOp",EDGE,"E29")])]})]});}
            var Q31;
            {var subQ0=sQuery(id+"F0.wireOp",EDGE,"E6.top");var subQ1=sQuery(id+"F0.wireOp",EDGE,"E1.0");var subQ4=sQuery(id+"F0.wireOp",EDGE,"E7.top");var subQ6=sQuery(id+"F0.wireOp",EDGE,"E9.left");var subQ22=sQuery(id+"F1.wireOp",EDGE,"E12");Q31=makeQuery(id+"F7.boolean.opBoolean","INTERSECT",EDGE,{"derivedFrom":[makeQuery(id+"F5.boolean.opBoolean","MERGE",FACE,{"derivedFrom":[makeQuery(id+"F3.boolean.opBoolean","SPLIT",FACE,{"disambiguationData":[TD([makeQuery(id+"F3.opExtrude","SWEPT_FACE",FACE,{"disambiguationData":[OSD([subQ6])]})])],"derivedFrom":makeQuery(id+"F2.opExtrude","SWEPT_FACE",FACE,{"disambiguationData":[OSD([subQ22])]})}),makeQuery(id+"F5.opExtrude","SWEPT_FACE",FACE,{"disambiguationData":[OSD([subQ1]),TDD([makeQuery(id+"F0.imprint","IMPRINT",EDGE,{"disambiguationData":[TD([[makeQuery(id+"F0.imprint","INTERSECT",VERTEX,{"disambiguationData":[OD(0.0)],"derivedFrom":[subQ1,subQ6]}),-1.0]])],"derivedFrom":subQ1})])]}),makeQuery(id+"F5.opExtrude","SWEPT_FACE",FACE,{"disambiguationData":[OSD([subQ1]),TDD([makeQuery(id+"F0.imprint","IMPRINT",EDGE,{"disambiguationData":[TD([[makeQuery(id+"F0.imprint","INTERSECT",VERTEX,{"disambiguationData":[OD(0.0)],"derivedFrom":[subQ1,subQ4]}),-1.0]])],"derivedFrom":subQ1})])]}),makeQuery(id+"F5.opExtrude","SWEPT_FACE",FACE,{"disambiguationData":[OSD([subQ1]),TDD([makeQuery(id+"F0.imprint","IMPRINT",EDGE,{"disambiguationData":[TD([[makeQuery(id+"F0.imprint","INTERSECT",VERTEX,{"disambiguationData":[OD(0.0)],"derivedFrom":[subQ1,subQ0]}),-1.0]])],"derivedFrom":subQ1})])]})]}),makeQuery(id+"F7.opExtrude","SWEPT_FACE",FACE,{"disambiguationData":[OSD([sQuery(id+"F6.wireOp",EDGE,"E29")])]})]});}
            var Q32;
            {var subQ0=sQuery(id+"F0.wireOp",EDGE,"E3.right");var subQ1=makeQuery(id+"F0.imprint","IMPRINT",EDGE,{"disambiguationData":[TD([[makeQuery(id+"F0.imprint","INTERSECT",VERTEX,{"disambiguationData":[OD(1.0)],"derivedFrom":[sQuery(id+"F0.wireOp",EDGE,"E1.0"),subQ0]}),1.0]])],"derivedFrom":subQ0});Q32=makeQuery(id+"F7.boolean.opBoolean","INTERSECT",EDGE,{"derivedFrom":[makeQuery(id+"F5.boolean.opBoolean","MERGE",FACE,{"derivedFrom":[makeQuery(id+"F3.opExtrude","SWEPT_FACE",FACE,{"disambiguationData":[OSD([subQ0]),TDD([subQ1])]}),makeQuery(id+"F5.opExtrude","SWEPT_FACE",FACE,{"disambiguationData":[OSD([subQ0]),TDD([subQ1])]})]}),makeQuery(id+"F7.opExtrude","SWEPT_FACE",FACE,{"disambiguationData":[OSD([sQuery(id+"F6.wireOp",EDGE,"E29")])]})]});}
            var Q33;
            {var subQ0=sQuery(id+"F0.wireOp",EDGE,"E3.right");var subQ1=sQuery(id+"F0.wireOp",EDGE,"E1.0");var subQ2=makeQuery(id+"F0.imprint","INTERSECT",VERTEX,{"disambiguationData":[OD(1.0)],"derivedFrom":[subQ1,subQ0]});var subQ3=sQuery(id+"F0.wireOp",EDGE,"E2.left");var subQ4=makeQuery(id+"F0.imprint","INTERSECT",VERTEX,{"disambiguationData":[OD(1.0)],"derivedFrom":[subQ1,subQ3]});var subQ21=sQuery(id+"F1.wireOp",EDGE,"E12");var subQ28=makeQuery(id+"F0.imprint","IMPRINT",EDGE,{"disambiguationData":[TD([[subQ4,1.0]])],"derivedFrom":subQ3});Q33=makeQuery(id+"F7.boolean.opBoolean","INTERSECT",EDGE,{"derivedFrom":[makeQuery(id+"F5.boolean.opBoolean","MERGE",FACE,{"derivedFrom":[makeQuery(id+"F3.boolean.opBoolean","SPLIT",FACE,{"disambiguationData":[TD([makeQuery(id+"F3.opExtrude","SWEPT_FACE",FACE,{"disambiguationData":[OSD([subQ3]),TDD([subQ28])]})])],"derivedFrom":makeQuery(id+"F2.opExtrude","SWEPT_FACE",FACE,{"disambiguationData":[OSD([subQ21])]})}),makeQuery(id+"F5.opExtrude","SWEPT_FACE",FACE,{"disambiguationData":[OSD([subQ1]),TDD([makeQuery(id+"F0.imprint","IMPRINT",EDGE,{"disambiguationData":[TD([[subQ2,-1.0]])],"derivedFrom":subQ1})])]})]}),makeQuery(id+"F7.opExtrude","SWEPT_FACE",FACE,{"disambiguationData":[OSD([sQuery(id+"F6.wireOp",EDGE,"E29")])]})]});}
            var Q34;
            {var subQ0=sQuery(id+"F0.wireOp",EDGE,"E6.top");var subQ1=sQuery(id+"F0.wireOp",EDGE,"E1.0");Q34=makeQuery(id+"F5.boolean.opBoolean","COPY",EDGE,{"derivedFrom":makeQuery(id+"F5.opExtrude","SWEPT_EDGE",EDGE,{"disambiguationData":[OSD([subQ1,subQ0]),TDD([makeQuery(id+"F0.imprint","INTERSECT",VERTEX,{"disambiguationData":[OD(0.0)],"derivedFrom":[subQ1,subQ0]})])]})});}
            var Q35;
            {var subQ1=sQuery(id+"F0.wireOp",EDGE,"E1.0");var subQ2=sQuery(id+"F0.wireOp",EDGE,"E6.bottom");var subQ3=makeQuery(id+"F0.imprint","INTERSECT",VERTEX,{"disambiguationData":[OD(1.0)],"derivedFrom":[subQ1,subQ2]});var subQ7=sQuery(id+"F0.wireOp",EDGE,"E9.left");var subQ9=sQuery(id+"F1.wireOp",EDGE,"E11");var subQ10=makeQuery(id+"F4.opExtrude","CAP_FACE",FACE,{"disambiguationData":[OSD([subQ9])],"isStart":false});var subQ11=sQuery(id+"F1.wireOp",EDGE,"E12");var subQ12=makeQuery(id+"F2.opExtrude","SWEPT_FACE",FACE,{"disambiguationData":[OSD([subQ11])]});Q35=makeQuery(id+"F5.boolean.opBoolean","SPLIT",EDGE,{"disambiguationData":[TD([makeQuery(id+"F5.opExtrude","SWEPT_FACE",FACE,{"disambiguationData":[OSD([subQ2]),TDD([makeQuery(id+"F0.imprint","IMPRINT",EDGE,{"disambiguationData":[TD([[subQ3,-1.0]])],"derivedFrom":subQ2})])]})])],"derivedFrom":makeQuery(id+"F4.boolean.opBoolean","INTERSECT",EDGE,{"derivedFrom":[makeQuery(id+"F3.boolean.opBoolean","SPLIT",FACE,{"disambiguationData":[TD([makeQuery(id+"F3.opExtrude","SWEPT_FACE",FACE,{"disambiguationData":[OSD([subQ7])]})])],"derivedFrom":subQ12}),subQ10]})});}
            var Q36;
            {var subQ0=sQuery(id+"F0.wireOp",EDGE,"E6.bottom");var subQ1=sQuery(id+"F0.wireOp",EDGE,"E1.0");Q36=makeQuery(id+"F5.boolean.opBoolean","COPY",EDGE,{"derivedFrom":makeQuery(id+"F5.opExtrude","SWEPT_EDGE",EDGE,{"disambiguationData":[OSD([subQ1,subQ0]),TDD([makeQuery(id+"F0.imprint","INTERSECT",VERTEX,{"disambiguationData":[OD(1.0)],"derivedFrom":[subQ1,subQ0]})])]})});}
            var Q37;
            {var subQ0=sQuery(id+"F0.wireOp",EDGE,"E6.top");var subQ1=sQuery(id+"F0.wireOp",EDGE,"E1.0");var subQ4=sQuery(id+"F0.wireOp",EDGE,"E7.top");var subQ6=sQuery(id+"F0.wireOp",EDGE,"E9.left");var subQ22=sQuery(id+"F1.wireOp",EDGE,"E12");Q37=makeQuery(id+"F7.boolean.opBoolean","INTERSECT",EDGE,{"disambiguationData":[OD(0.0)],"derivedFrom":[makeQuery(id+"F5.boolean.opBoolean","MERGE",FACE,{"derivedFrom":[makeQuery(id+"F3.boolean.opBoolean","SPLIT",FACE,{"disambiguationData":[TD([makeQuery(id+"F3.opExtrude","SWEPT_FACE",FACE,{"disambiguationData":[OSD([subQ6])]})])],"derivedFrom":makeQuery(id+"F2.opExtrude","SWEPT_FACE",FACE,{"disambiguationData":[OSD([subQ22])]})}),makeQuery(id+"F5.opExtrude","SWEPT_FACE",FACE,{"disambiguationData":[OSD([subQ1]),TDD([makeQuery(id+"F0.imprint","IMPRINT",EDGE,{"disambiguationData":[TD([[makeQuery(id+"F0.imprint","INTERSECT",VERTEX,{"disambiguationData":[OD(0.0)],"derivedFrom":[subQ1,subQ6]}),-1.0]])],"derivedFrom":subQ1})])]}),makeQuery(id+"F5.opExtrude","SWEPT_FACE",FACE,{"disambiguationData":[OSD([subQ1]),TDD([makeQuery(id+"F0.imprint","IMPRINT",EDGE,{"disambiguationData":[TD([[makeQuery(id+"F0.imprint","INTERSECT",VERTEX,{"disambiguationData":[OD(0.0)],"derivedFrom":[subQ1,subQ4]}),-1.0]])],"derivedFrom":subQ1})])]}),makeQuery(id+"F5.opExtrude","SWEPT_FACE",FACE,{"disambiguationData":[OSD([subQ1]),TDD([makeQuery(id+"F0.imprint","IMPRINT",EDGE,{"disambiguationData":[TD([[makeQuery(id+"F0.imprint","INTERSECT",VERTEX,{"disambiguationData":[OD(0.0)],"derivedFrom":[subQ1,subQ0]}),-1.0]])],"derivedFrom":subQ1})])]})]}),makeQuery(id+"F7.opExtrude","SWEPT_FACE",FACE,{"disambiguationData":[OSD([sQuery(id+"F6.wireOp",EDGE,"E30")])]})]});}
            var Q38;
            {var subQ0=sQuery(id+"F0.wireOp",EDGE,"E7.bottom");Q38=makeQuery(id+"F7.boolean.opBoolean","INTERSECT",EDGE,{"derivedFrom":[makeQuery(id+"F5.boolean.opBoolean","COPY",FACE,{"derivedFrom":makeQuery(id+"F5.opExtrude","SWEPT_FACE",FACE,{"disambiguationData":[OSD([subQ0]),TDD([makeQuery(id+"F0.imprint","IMPRINT",EDGE,{"disambiguationData":[TD([[makeQuery(id+"F0.imprint","INTERSECT",VERTEX,{"disambiguationData":[OD(0.0)],"derivedFrom":[sQuery(id+"F0.wireOp",EDGE,"E1.0"),subQ0]}),-1.0]])],"derivedFrom":subQ0})])]})}),makeQuery(id+"F7.opExtrude","SWEPT_FACE",FACE,{"disambiguationData":[OSD([sQuery(id+"F6.wireOp",EDGE,"E30")])]})]});}
            var Q39;
            Q39=makeQuery(id+"F7.boolean.opBoolean","INTERSECT",EDGE,{"derivedFrom":[makeQuery(id+"F4.opExtrude","CAP_FACE",FACE,{"disambiguationData":[OSD([sQuery(id+"F1.wireOp",EDGE,"E11")])],"isStart":false}),makeQuery(id+"F7.opExtrude","SWEPT_FACE",FACE,{"disambiguationData":[OSD([sQuery(id+"F6.wireOp",EDGE,"E30")])]})]});
            var Q40;
            Q40=makeQuery(id+"F7.boolean.opBoolean","INTERSECT",EDGE,{"derivedFrom":[makeQuery(id+"F5.boolean.opBoolean","COPY",FACE,{"derivedFrom":makeQuery(id+"F5.opExtrude","SWEPT_FACE",FACE,{"disambiguationData":[OSD([sQuery(id+"F0.wireOp",EDGE,"E7.top")])]})}),makeQuery(id+"F7.opExtrude","SWEPT_FACE",FACE,{"disambiguationData":[OSD([sQuery(id+"F6.wireOp",EDGE,"E30")])]})]});
            var Q41;
            {var subQ0=sQuery(id+"F0.wireOp",EDGE,"E6.top");var subQ1=sQuery(id+"F0.wireOp",EDGE,"E1.0");var subQ4=sQuery(id+"F0.wireOp",EDGE,"E7.top");var subQ6=sQuery(id+"F0.wireOp",EDGE,"E9.left");var subQ22=sQuery(id+"F1.wireOp",EDGE,"E12");Q41=makeQuery(id+"F7.boolean.opBoolean","INTERSECT",EDGE,{"disambiguationData":[OD(1.0)],"derivedFrom":[makeQuery(id+"F5.boolean.opBoolean","MERGE",FACE,{"derivedFrom":[makeQuery(id+"F3.boolean.opBoolean","SPLIT",FACE,{"disambiguationData":[TD([makeQuery(id+"F3.opExtrude","SWEPT_FACE",FACE,{"disambiguationData":[OSD([subQ6])]})])],"derivedFrom":makeQuery(id+"F2.opExtrude","SWEPT_FACE",FACE,{"disambiguationData":[OSD([subQ22])]})}),makeQuery(id+"F5.opExtrude","SWEPT_FACE",FACE,{"disambiguationData":[OSD([subQ1]),TDD([makeQuery(id+"F0.imprint","IMPRINT",EDGE,{"disambiguationData":[TD([[makeQuery(id+"F0.imprint","INTERSECT",VERTEX,{"disambiguationData":[OD(0.0)],"derivedFrom":[subQ1,subQ6]}),-1.0]])],"derivedFrom":subQ1})])]}),makeQuery(id+"F5.opExtrude","SWEPT_FACE",FACE,{"disambiguationData":[OSD([subQ1]),TDD([makeQuery(id+"F0.imprint","IMPRINT",EDGE,{"disambiguationData":[TD([[makeQuery(id+"F0.imprint","INTERSECT",VERTEX,{"disambiguationData":[OD(0.0)],"derivedFrom":[subQ1,subQ4]}),-1.0]])],"derivedFrom":subQ1})])]}),makeQuery(id+"F5.opExtrude","SWEPT_FACE",FACE,{"disambiguationData":[OSD([subQ1]),TDD([makeQuery(id+"F0.imprint","IMPRINT",EDGE,{"disambiguationData":[TD([[makeQuery(id+"F0.imprint","INTERSECT",VERTEX,{"disambiguationData":[OD(0.0)],"derivedFrom":[subQ1,subQ0]}),-1.0]])],"derivedFrom":subQ1})])]})]}),makeQuery(id+"F7.opExtrude","SWEPT_FACE",FACE,{"disambiguationData":[OSD([sQuery(id+"F6.wireOp",EDGE,"E30")])]})]});}
            var Q42;
            Q42=makeQuery(id+"F7.boolean.opBoolean","INTERSECT",EDGE,{"derivedFrom":[makeQuery(id+"F3.opExtrude","SWEPT_FACE",FACE,{"disambiguationData":[OSD([sQuery(id+"F0.wireOp",EDGE,"E8.left")])]}),makeQuery(id+"F7.opExtrude","SWEPT_FACE",FACE,{"disambiguationData":[OSD([sQuery(id+"F6.wireOp",EDGE,"E25")])]})]});
            var Q43;
            {var subQ5=sQuery(id+"F0.wireOp",EDGE,"E8.left");var subQ16=sQuery(id+"F1.wireOp",EDGE,"E12");Q43=makeQuery(id+"F7.boolean.opBoolean","INTERSECT",EDGE,{"derivedFrom":[makeQuery(id+"F3.boolean.opBoolean","SPLIT",FACE,{"disambiguationData":[TD([makeQuery(id+"F3.opExtrude","SWEPT_FACE",FACE,{"disambiguationData":[OSD([subQ5])]})])],"derivedFrom":makeQuery(id+"F2.opExtrude","SWEPT_FACE",FACE,{"disambiguationData":[OSD([subQ16])]})}),makeQuery(id+"F7.opExtrude","SWEPT_FACE",FACE,{"disambiguationData":[OSD([sQuery(id+"F6.wireOp",EDGE,"E25")])]})]});}
            var Q44;
            {var subQ0=sQuery(id+"F0.wireOp",EDGE,"E8.right");Q44=makeQuery(id+"F7.boolean.opBoolean","INTERSECT",EDGE,{"derivedFrom":[makeQuery(id+"F5.boolean.opBoolean","MERGE",FACE,{"derivedFrom":[makeQuery(id+"F3.opExtrude","SWEPT_FACE",FACE,{"disambiguationData":[OSD([subQ0])]}),makeQuery(id+"F5.opExtrude","SWEPT_FACE",FACE,{"disambiguationData":[OSD([subQ0]),TDD([makeQuery(id+"F0.imprint","IMPRINT",EDGE,{"disambiguationData":[TD([[makeQuery(id+"F0.imprint","INTERSECT",VERTEX,{"disambiguationData":[OD(0.0)],"derivedFrom":[sQuery(id+"F0.wireOp",EDGE,"E1.0"),subQ0]}),-1.0]])],"derivedFrom":subQ0})])]})]}),makeQuery(id+"F7.opExtrude","SWEPT_FACE",FACE,{"disambiguationData":[OSD([sQuery(id+"F6.wireOp",EDGE,"E25")])]})]});}
            var Q45;
            {var subQ0=sQuery(id+"F0.wireOp",EDGE,"E2.left");var subQ1=sQuery(id+"F0.wireOp",EDGE,"E1.0");var subQ2=makeQuery(id+"F0.imprint","INTERSECT",VERTEX,{"disambiguationData":[OD(0.0)],"derivedFrom":[subQ1,subQ0]});var subQ3=sQuery(id+"F0.wireOp",EDGE,"E8.right");var subQ16=sQuery(id+"F1.wireOp",EDGE,"E12");Q45=makeQuery(id+"F7.boolean.opBoolean","INTERSECT",EDGE,{"derivedFrom":[makeQuery(id+"F5.boolean.opBoolean","MERGE",FACE,{"derivedFrom":[makeQuery(id+"F3.boolean.opBoolean","SPLIT",FACE,{"disambiguationData":[TD([makeQuery(id+"F3.opExtrude","SWEPT_FACE",FACE,{"disambiguationData":[OSD([subQ3])]})])],"derivedFrom":makeQuery(id+"F2.opExtrude","SWEPT_FACE",FACE,{"disambiguationData":[OSD([subQ16])]})}),makeQuery(id+"F5.opExtrude","SWEPT_FACE",FACE,{"disambiguationData":[OSD([subQ1]),TDD([makeQuery(id+"F0.imprint","IMPRINT",EDGE,{"disambiguationData":[TD([[subQ2,-1.0]])],"derivedFrom":subQ1})])]})]}),makeQuery(id+"F7.opExtrude","SWEPT_FACE",FACE,{"disambiguationData":[OSD([sQuery(id+"F6.wireOp",EDGE,"E25")])]})]});}
            var Q46;
            {var subQ3=sQuery(id+"F0.wireOp",EDGE,"E1.0");var subQ8=sQuery(id+"F0.wireOp",EDGE,"E2.right");var subQ11=makeQuery(id+"F0.imprint","INTERSECT",VERTEX,{"disambiguationData":[OD(0.0)],"derivedFrom":[subQ3,subQ8]});var subQ12=makeQuery(id+"F0.imprint","IMPRINT",EDGE,{"disambiguationData":[TD([[subQ11,-1.0]])],"derivedFrom":subQ8});var subQ20=sQuery(id+"F1.wireOp",EDGE,"E12");Q46=makeQuery(id+"F7.boolean.opBoolean","INTERSECT",EDGE,{"derivedFrom":[makeQuery(id+"F3.boolean.opBoolean","SPLIT",FACE,{"disambiguationData":[TD([makeQuery(id+"F3.opExtrude","SWEPT_FACE",FACE,{"disambiguationData":[OSD([subQ8]),TDD([subQ12])]})])],"derivedFrom":makeQuery(id+"F2.opExtrude","SWEPT_FACE",FACE,{"disambiguationData":[OSD([subQ20])]})}),makeQuery(id+"F7.opExtrude","SWEPT_FACE",FACE,{"disambiguationData":[OSD([sQuery(id+"F6.wireOp",EDGE,"E26")])]})]});}
            var Q47;
            {var subQ0=sQuery(id+"F0.wireOp",EDGE,"E3.left");Q47=makeQuery(id+"F7.boolean.opBoolean","INTERSECT",EDGE,{"derivedFrom":[makeQuery(id+"F3.opExtrude","SWEPT_FACE",FACE,{"disambiguationData":[OSD([subQ0]),TDD([makeQuery(id+"F0.imprint","IMPRINT",EDGE,{"disambiguationData":[TD([[makeQuery(id+"F0.imprint","INTERSECT",VERTEX,{"disambiguationData":[OD(0.0)],"derivedFrom":[sQuery(id+"F0.wireOp",EDGE,"E1.0"),subQ0]}),-1.0]])],"derivedFrom":subQ0})])]}),makeQuery(id+"F7.opExtrude","SWEPT_FACE",FACE,{"disambiguationData":[OSD([sQuery(id+"F6.wireOp",EDGE,"E26")])]})]});}
            var Q48;
            {var subQ0=sQuery(id+"F0.wireOp",EDGE,"E3.right");var subQ1=sQuery(id+"F0.wireOp",EDGE,"E1.0");var subQ2=makeQuery(id+"F0.imprint","INTERSECT",VERTEX,{"disambiguationData":[OD(0.0)],"derivedFrom":[subQ1,subQ0]});var subQ3=sQuery(id+"F0.wireOp",EDGE,"E6.bottom");var subQ21=sQuery(id+"F1.wireOp",EDGE,"E12");Q48=makeQuery(id+"F7.boolean.opBoolean","INTERSECT",EDGE,{"derivedFrom":[makeQuery(id+"F5.boolean.opBoolean","MERGE",FACE,{"derivedFrom":[makeQuery(id+"F3.boolean.opBoolean","SPLIT",FACE,{"disambiguationData":[TD([makeQuery(id+"F3.opExtrude","SWEPT_FACE",FACE,{"disambiguationData":[OSD([subQ3])]})])],"derivedFrom":makeQuery(id+"F2.opExtrude","SWEPT_FACE",FACE,{"disambiguationData":[OSD([subQ21])]})}),makeQuery(id+"F5.opExtrude","SWEPT_FACE",FACE,{"disambiguationData":[OSD([subQ1]),TDD([makeQuery(id+"F0.imprint","IMPRINT",EDGE,{"disambiguationData":[TD([[subQ2,1.0]])],"derivedFrom":subQ1})])]})]}),makeQuery(id+"F7.opExtrude","SWEPT_FACE",FACE,{"disambiguationData":[OSD([sQuery(id+"F6.wireOp",EDGE,"E26")])]})]});}
            var Q49;
            {var subQ0=sQuery(id+"F0.wireOp",EDGE,"E3.right");var subQ1=makeQuery(id+"F0.imprint","IMPRINT",EDGE,{"disambiguationData":[TD([[makeQuery(id+"F0.imprint","INTERSECT",VERTEX,{"disambiguationData":[OD(0.0)],"derivedFrom":[sQuery(id+"F0.wireOp",EDGE,"E1.0"),subQ0]}),-1.0]])],"derivedFrom":subQ0});Q49=makeQuery(id+"F7.boolean.opBoolean","INTERSECT",EDGE,{"derivedFrom":[makeQuery(id+"F5.boolean.opBoolean","MERGE",FACE,{"derivedFrom":[makeQuery(id+"F3.opExtrude","SWEPT_FACE",FACE,{"disambiguationData":[OSD([subQ0]),TDD([subQ1])]}),makeQuery(id+"F5.opExtrude","SWEPT_FACE",FACE,{"disambiguationData":[OSD([subQ0]),TDD([subQ1])]})]}),makeQuery(id+"F7.opExtrude","SWEPT_FACE",FACE,{"disambiguationData":[OSD([sQuery(id+"F6.wireOp",EDGE,"E26")])]})]});}
            var Q50;
            {var subQ0=sQuery(id+"F0.wireOp",EDGE,"E8.right");var subQ1=sQuery(id+"F0.wireOp",EDGE,"E1.0");var subQ19=sQuery(id+"F1.wireOp",EDGE,"E12");var subQ44=sQuery(id+"F0.wireOp",EDGE,"E7.top");Q50=makeQuery(id+"F7.boolean.opBoolean","INTERSECT",EDGE,{"derivedFrom":[makeQuery(id+"F5.boolean.opBoolean","MERGE",FACE,{"derivedFrom":[makeQuery(id+"F3.boolean.opBoolean","SPLIT",FACE,{"disambiguationData":[TD([makeQuery(id+"F3.opExtrude","SWEPT_FACE",FACE,{"disambiguationData":[OSD([subQ44])]})])],"derivedFrom":makeQuery(id+"F2.opExtrude","SWEPT_FACE",FACE,{"disambiguationData":[OSD([subQ19])]})}),makeQuery(id+"F5.opExtrude","SWEPT_FACE",FACE,{"disambiguationData":[OSD([subQ1]),TDD([makeQuery(id+"F0.imprint","IMPRINT",EDGE,{"disambiguationData":[TD([[makeQuery(id+"F0.imprint","INTERSECT",VERTEX,{"disambiguationData":[OD(1.0)],"derivedFrom":[subQ1,subQ0]}),-1.0]])],"derivedFrom":subQ1})])]})]}),makeQuery(id+"F7.opExtrude","SWEPT_FACE",FACE,{"disambiguationData":[OSD([sQuery(id+"F6.wireOp",EDGE,"E27")])]})]});}
            var Q51;
            Q51=makeQuery(id+"F7.boolean.opBoolean","INTERSECT",EDGE,{"derivedFrom":[makeQuery(id+"F3.opExtrude","SWEPT_FACE",FACE,{"disambiguationData":[OSD([sQuery(id+"F0.wireOp",EDGE,"E7.top")])]}),makeQuery(id+"F7.opExtrude","SWEPT_FACE",FACE,{"disambiguationData":[OSD([sQuery(id+"F6.wireOp",EDGE,"E27")])]})]});
            fillet(context, id + "F8", {"entities" : qUnion([Q0, Q1, Q2, Q3, Q4, Q5, Q6, Q7, Q8, Q9, Q10, Q11, Q12, Q13, Q14, Q15, Q16, Q17, Q18, Q19, Q20, Q21, Q22, Q23, Q24, Q25, Q26, Q27, Q28, Q29, Q30, Q31, Q32, Q33, Q34, Q35, Q36, Q37, Q38, Q39, Q40, Q41, Q42, Q43, Q44, Q45, Q46, Q47, Q48, Q49, Q50, Q51]), "radius" : 1 * mm, "tangentPropagation" : true, "allowEdgeOverflow" : false});
        }
        {
            var Q0;
            {var subQ0=sQuery(id+"F6.wireOp",EDGE,"E31");var subQ1=sQuery(id+"F6.wireOp",EDGE,"E13");var subQ2=makeQuery(id+"F6.imprint","INTERSECT",VERTEX,{"disambiguationData":[OD(0.0)],"derivedFrom":[subQ1,subQ0]});Q0=makeQuery(id+"F6.imprint","IMPRINT",FACE,{"disambiguationData":[TD([[makeQuery(id+"F6.imprint","IMPRINT",EDGE,{"disambiguationData":[TD([[subQ2,-1.0]])],"derivedFrom":subQ1}),-1.0]])]});}
            var Q1;
            {var subQ0=sQuery(id+"F6.wireOp",EDGE,"E31");var subQ1=sQuery(id+"F6.wireOp",EDGE,"E13");var subQ2=makeQuery(id+"F6.imprint","INTERSECT",VERTEX,{"disambiguationData":[OD(0.0)],"derivedFrom":[subQ1,subQ0]});Q1=makeQuery(id+"F6.imprint","IMPRINT",FACE,{"disambiguationData":[TD([[makeQuery(id+"F6.imprint","IMPRINT",EDGE,{"disambiguationData":[TD([[subQ2,-1.0]])],"derivedFrom":subQ1}),1.0]])]});}
            var Q2;
            {var subQ0=sQuery(id+"F6.wireOp",EDGE,"E32");var subQ1=sQuery(id+"F6.wireOp",EDGE,"E13");var subQ2=makeQuery(id+"F6.imprint","INTERSECT",VERTEX,{"disambiguationData":[OD(0.0)],"derivedFrom":[subQ1,subQ0]});Q2=makeQuery(id+"F6.imprint","IMPRINT",FACE,{"disambiguationData":[TD([[makeQuery(id+"F6.imprint","IMPRINT",EDGE,{"disambiguationData":[TD([[subQ2,-1.0]])],"derivedFrom":subQ1}),-1.0]])]});}
            var Q3;
            {var subQ0=sQuery(id+"F6.wireOp",EDGE,"E32");var subQ1=sQuery(id+"F6.wireOp",EDGE,"E13");var subQ2=makeQuery(id+"F6.imprint","INTERSECT",VERTEX,{"disambiguationData":[OD(0.0)],"derivedFrom":[subQ1,subQ0]});Q3=makeQuery(id+"F6.imprint","IMPRINT",FACE,{"disambiguationData":[TD([[makeQuery(id+"F6.imprint","IMPRINT",EDGE,{"disambiguationData":[TD([[subQ2,-1.0]])],"derivedFrom":subQ1}),1.0]])]});}
            var Q4;
            {var subQ0=sQuery(id+"F6.wireOp",EDGE,"E33");var subQ1=sQuery(id+"F6.wireOp",EDGE,"E13");var subQ2=makeQuery(id+"F6.imprint","INTERSECT",VERTEX,{"disambiguationData":[OD(0.0)],"derivedFrom":[subQ1,subQ0]});Q4=makeQuery(id+"F6.imprint","IMPRINT",FACE,{"disambiguationData":[TD([[makeQuery(id+"F6.imprint","IMPRINT",EDGE,{"disambiguationData":[TD([[subQ2,-1.0]])],"derivedFrom":subQ1}),1.0]])]});}
            var Q5;
            {var subQ0=sQuery(id+"F6.wireOp",EDGE,"E33");var subQ1=sQuery(id+"F6.wireOp",EDGE,"E13");var subQ2=makeQuery(id+"F6.imprint","INTERSECT",VERTEX,{"disambiguationData":[OD(0.0)],"derivedFrom":[subQ1,subQ0]});Q5=makeQuery(id+"F6.imprint","IMPRINT",FACE,{"disambiguationData":[TD([[makeQuery(id+"F6.imprint","IMPRINT",EDGE,{"disambiguationData":[TD([[subQ2,-1.0]])],"derivedFrom":subQ1}),-1.0]])]});}
            var Q6;
            {var subQ0=sQuery(id+"F6.wireOp",EDGE,"E34");var subQ1=sQuery(id+"F6.wireOp",EDGE,"E13");var subQ2=makeQuery(id+"F6.imprint","INTERSECT",VERTEX,{"disambiguationData":[OD(0.0)],"derivedFrom":[subQ1,subQ0]});Q6=makeQuery(id+"F6.imprint","IMPRINT",FACE,{"disambiguationData":[TD([[makeQuery(id+"F6.imprint","IMPRINT",EDGE,{"disambiguationData":[TD([[subQ2,-1.0]])],"derivedFrom":subQ1}),1.0]])]});}
            var Q7;
            {var subQ0=sQuery(id+"F6.wireOp",EDGE,"E34");var subQ1=sQuery(id+"F6.wireOp",EDGE,"E13");var subQ2=makeQuery(id+"F6.imprint","INTERSECT",VERTEX,{"disambiguationData":[OD(0.0)],"derivedFrom":[subQ1,subQ0]});Q7=makeQuery(id+"F6.imprint","IMPRINT",FACE,{"disambiguationData":[TD([[makeQuery(id+"F6.imprint","IMPRINT",EDGE,{"disambiguationData":[TD([[subQ2,-1.0]])],"derivedFrom":subQ1}),-1.0]])]});}
            var Q8;
            {var subQ1=sQuery(id+"F6.wireOp",EDGE,"E36.bottom");Q8=makeQuery(id+"F6.imprint","IMPRINT",FACE,{"disambiguationData":[TD([[makeQuery(id+"F6.imprint","IMPRINT",EDGE,{"derivedFrom":subQ1}),-1.0]])]});}
            var Q9;
            {var subQ0=sQuery(id+"F6.wireOp",EDGE,"E36.top");var subQ1=sQuery(id+"F6.wireOp",EDGE,"E13");var subQ2=makeQuery(id+"F6.imprint","INTERSECT",VERTEX,{"derivedFrom":[subQ1,subQ0]});Q9=makeQuery(id+"F6.imprint","IMPRINT",FACE,{"disambiguationData":[TD([[makeQuery(id+"F6.imprint","IMPRINT",EDGE,{"disambiguationData":[TD([[subQ2,-1.0]])],"derivedFrom":subQ1}),1.0]])]});}
            var Q10;
            {var subQ0=sQuery(id+"F6.wireOp",EDGE,"E35");var subQ1=sQuery(id+"F6.wireOp",EDGE,"E13");var subQ2=makeQuery(id+"F6.imprint","INTERSECT",VERTEX,{"disambiguationData":[OD(0.0)],"derivedFrom":[subQ1,subQ0]});Q10=makeQuery(id+"F6.imprint","IMPRINT",FACE,{"disambiguationData":[TD([[makeQuery(id+"F6.imprint","IMPRINT",EDGE,{"disambiguationData":[TD([[subQ2,-1.0]])],"derivedFrom":subQ1}),-1.0]])]});}
            var Q11;
            {var subQ0=sQuery(id+"F6.wireOp",EDGE,"E35");var subQ1=sQuery(id+"F6.wireOp",EDGE,"E13");var subQ2=makeQuery(id+"F6.imprint","INTERSECT",VERTEX,{"disambiguationData":[OD(0.0)],"derivedFrom":[subQ1,subQ0]});Q11=makeQuery(id+"F6.imprint","IMPRINT",FACE,{"disambiguationData":[TD([[makeQuery(id+"F6.imprint","IMPRINT",EDGE,{"disambiguationData":[TD([[subQ2,-1.0]])],"derivedFrom":subQ1}),1.0]])]});}
            extrude(context, id + "F9", {"entities" : qUnion([Q0, Q1, Q2, Q3, Q4, Q5, Q6, Q7, Q8, Q9, Q10, Q11]), "operationType" : NewBodyOperationType.ADD, "depth" : 11 * mm, "offsetDistance" : 25 * mm, "hasDraft" : true, "draftAngle" : .9 * degree, "draftPullDirection" : true});
        }
        {
            var Q0;
            Q0=makeQuery(id+"F9.opExtrude","CAP_EDGE",EDGE,{"disambiguationData":[OSD([sQuery(id+"F6.wireOp",EDGE,"E35")])],"isStart":false});
            var Q1;
            Q1=makeQuery(id+"F9.opExtrude","CAP_FACE",FACE,{"disambiguationData":[OSD([sQuery(id+"F6.wireOp",EDGE,"E31")])],"isStart":false});
            var Q2;
            Q2=makeQuery(id+"F9.opExtrude","CAP_FACE",FACE,{"disambiguationData":[OSD([sQuery(id+"F6.wireOp",EDGE,"E32")])],"isStart":false});
            var Q3;
            Q3=makeQuery(id+"F9.opExtrude","CAP_FACE",FACE,{"disambiguationData":[OSD([sQuery(id+"F6.wireOp",EDGE,"E33")])],"isStart":false});
            var Q4;
            Q4=makeQuery(id+"F9.opExtrude","CAP_FACE",FACE,{"disambiguationData":[OSD([sQuery(id+"F6.wireOp",EDGE,"E34")])],"isStart":false});
            var Q5;
            Q5=makeQuery(id+"F9.opExtrude","CAP_EDGE",EDGE,{"disambiguationData":[OSD([sQuery(id+"F6.wireOp",EDGE,"E36.left")])],"isStart":false});
            var Q6;
            Q6=makeQuery(id+"F9.opExtrude","CAP_EDGE",EDGE,{"disambiguationData":[OSD([sQuery(id+"F6.wireOp",EDGE,"E36.right")])],"isStart":false});
            var Q7;
            Q7=makeQuery(id+"F9.opExtrude","CAP_EDGE",EDGE,{"disambiguationData":[OSD([sQuery(id+"F6.wireOp",EDGE,"E36.bottom")])],"isStart":false});
            var Q8;
            Q8=makeQuery(id+"F9.opExtrude","CAP_EDGE",EDGE,{"disambiguationData":[OSD([sQuery(id+"F6.wireOp",EDGE,"E36.top")])],"isStart":false});
            fillet(context, id + "F10", {"entities" : qUnion([Q0, Q1, Q2, Q3, Q4, Q5, Q6, Q7, Q8]), "radius" : .45 * mm, "tangentPropagation" : true, "allowEdgeOverflow" : false});
        }
        {
            var Q0;
            {var subQ0=sQuery(id+"F6.wireOp",EDGE,"E35");var subQ1=sQuery(id+"F6.wireOp",EDGE,"E13");var subQ2=makeQuery(id+"F6.imprint","INTERSECT",VERTEX,{"disambiguationData":[OD(0.0)],"derivedFrom":[subQ1,subQ0]});Q0=makeQuery(id+"F6.imprint","IMPRINT",FACE,{"disambiguationData":[TD([[makeQuery(id+"F6.imprint","IMPRINT",EDGE,{"disambiguationData":[TD([[subQ2,-1.0]])],"derivedFrom":subQ1}),-1.0]])]});}
            var Q1;
            {var subQ0=sQuery(id+"F6.wireOp",EDGE,"E35");var subQ1=sQuery(id+"F6.wireOp",EDGE,"E13");var subQ2=makeQuery(id+"F6.imprint","INTERSECT",VERTEX,{"disambiguationData":[OD(0.0)],"derivedFrom":[subQ1,subQ0]});Q1=makeQuery(id+"F6.imprint","IMPRINT",FACE,{"disambiguationData":[TD([[makeQuery(id+"F6.imprint","IMPRINT",EDGE,{"disambiguationData":[TD([[subQ2,-1.0]])],"derivedFrom":subQ1}),1.0]])]});}
            var Q2;
            {var subQ1=sQuery(id+"F6.wireOp",EDGE,"E36.bottom");Q2=makeQuery(id+"F6.imprint","IMPRINT",FACE,{"disambiguationData":[TD([[makeQuery(id+"F6.imprint","IMPRINT",EDGE,{"derivedFrom":subQ1}),-1.0]])]});}
            var Q3;
            {var subQ0=sQuery(id+"F6.wireOp",EDGE,"E36.top");var subQ1=sQuery(id+"F6.wireOp",EDGE,"E13");var subQ2=makeQuery(id+"F6.imprint","INTERSECT",VERTEX,{"derivedFrom":[subQ1,subQ0]});Q3=makeQuery(id+"F6.imprint","IMPRINT",FACE,{"disambiguationData":[TD([[makeQuery(id+"F6.imprint","IMPRINT",EDGE,{"disambiguationData":[TD([[subQ2,-1.0]])],"derivedFrom":subQ1}),1.0]])]});}
            var Q4;
            {var subQ0=sQuery(id+"F6.wireOp",EDGE,"E34");var subQ1=sQuery(id+"F6.wireOp",EDGE,"E13");var subQ2=makeQuery(id+"F6.imprint","INTERSECT",VERTEX,{"disambiguationData":[OD(0.0)],"derivedFrom":[subQ1,subQ0]});Q4=makeQuery(id+"F6.imprint","IMPRINT",FACE,{"disambiguationData":[TD([[makeQuery(id+"F6.imprint","IMPRINT",EDGE,{"disambiguationData":[TD([[subQ2,-1.0]])],"derivedFrom":subQ1}),1.0]])]});}
            var Q5;
            {var subQ0=sQuery(id+"F6.wireOp",EDGE,"E34");var subQ1=sQuery(id+"F6.wireOp",EDGE,"E13");var subQ2=makeQuery(id+"F6.imprint","INTERSECT",VERTEX,{"disambiguationData":[OD(0.0)],"derivedFrom":[subQ1,subQ0]});Q5=makeQuery(id+"F6.imprint","IMPRINT",FACE,{"disambiguationData":[TD([[makeQuery(id+"F6.imprint","IMPRINT",EDGE,{"disambiguationData":[TD([[subQ2,-1.0]])],"derivedFrom":subQ1}),-1.0]])]});}
            var Q6;
            {var subQ0=sQuery(id+"F6.wireOp",EDGE,"E33");var subQ1=sQuery(id+"F6.wireOp",EDGE,"E13");var subQ2=makeQuery(id+"F6.imprint","INTERSECT",VERTEX,{"disambiguationData":[OD(0.0)],"derivedFrom":[subQ1,subQ0]});Q6=makeQuery(id+"F6.imprint","IMPRINT",FACE,{"disambiguationData":[TD([[makeQuery(id+"F6.imprint","IMPRINT",EDGE,{"disambiguationData":[TD([[subQ2,-1.0]])],"derivedFrom":subQ1}),1.0]])]});}
            var Q7;
            {var subQ0=sQuery(id+"F6.wireOp",EDGE,"E33");var subQ1=sQuery(id+"F6.wireOp",EDGE,"E13");var subQ2=makeQuery(id+"F6.imprint","INTERSECT",VERTEX,{"disambiguationData":[OD(0.0)],"derivedFrom":[subQ1,subQ0]});Q7=makeQuery(id+"F6.imprint","IMPRINT",FACE,{"disambiguationData":[TD([[makeQuery(id+"F6.imprint","IMPRINT",EDGE,{"disambiguationData":[TD([[subQ2,-1.0]])],"derivedFrom":subQ1}),-1.0]])]});}
            var Q8;
            {var subQ0=sQuery(id+"F6.wireOp",EDGE,"E32");var subQ1=sQuery(id+"F6.wireOp",EDGE,"E13");var subQ2=makeQuery(id+"F6.imprint","INTERSECT",VERTEX,{"disambiguationData":[OD(0.0)],"derivedFrom":[subQ1,subQ0]});Q8=makeQuery(id+"F6.imprint","IMPRINT",FACE,{"disambiguationData":[TD([[makeQuery(id+"F6.imprint","IMPRINT",EDGE,{"disambiguationData":[TD([[subQ2,-1.0]])],"derivedFrom":subQ1}),1.0]])]});}
            var Q9;
            {var subQ0=sQuery(id+"F6.wireOp",EDGE,"E32");var subQ1=sQuery(id+"F6.wireOp",EDGE,"E13");var subQ2=makeQuery(id+"F6.imprint","INTERSECT",VERTEX,{"disambiguationData":[OD(0.0)],"derivedFrom":[subQ1,subQ0]});Q9=makeQuery(id+"F6.imprint","IMPRINT",FACE,{"disambiguationData":[TD([[makeQuery(id+"F6.imprint","IMPRINT",EDGE,{"disambiguationData":[TD([[subQ2,-1.0]])],"derivedFrom":subQ1}),-1.0]])]});}
            var Q10;
            {var subQ0=sQuery(id+"F6.wireOp",EDGE,"E31");var subQ1=sQuery(id+"F6.wireOp",EDGE,"E13");var subQ2=makeQuery(id+"F6.imprint","INTERSECT",VERTEX,{"disambiguationData":[OD(0.0)],"derivedFrom":[subQ1,subQ0]});Q10=makeQuery(id+"F6.imprint","IMPRINT",FACE,{"disambiguationData":[TD([[makeQuery(id+"F6.imprint","IMPRINT",EDGE,{"disambiguationData":[TD([[subQ2,-1.0]])],"derivedFrom":subQ1}),-1.0]])]});}
            var Q11;
            {var subQ0=sQuery(id+"F6.wireOp",EDGE,"E31");var subQ1=sQuery(id+"F6.wireOp",EDGE,"E13");var subQ2=makeQuery(id+"F6.imprint","INTERSECT",VERTEX,{"disambiguationData":[OD(0.0)],"derivedFrom":[subQ1,subQ0]});Q11=makeQuery(id+"F6.imprint","IMPRINT",FACE,{"disambiguationData":[TD([[makeQuery(id+"F6.imprint","IMPRINT",EDGE,{"disambiguationData":[TD([[subQ2,-1.0]])],"derivedFrom":subQ1}),1.0]])]});}
            extrude(context, id + "F11", {"entities" : qUnion([Q0, Q1, Q2, Q3, Q4, Q5, Q6, Q7, Q8, Q9, Q10, Q11]), "operationType" : NewBodyOperationType.REMOVE, "depth" : 3 * mm, "offsetDistance" : 25 * mm});
        }
        {
            var Q0;
            Q0=qCreatedBy(makeId("Top.planeOp"),FACE);
            var sketch = newSketch(context, id + "F12", { "sketchPlane" : qUnion([Q0])});
            skCircle(sketch, "E37", {"center": v(0, 0) * mm, "radius": 17.33 * mm});
            skSolve(sketch);
        }
        {
            var Q0;
            Q0=makeQuery(id+"F12.imprint","IMPRINT",FACE,{"disambiguationData":[TD([[makeQuery(id+"F12.imprint","IMPRINT",EDGE,{"derivedFrom":sQuery(id+"F12.wireOp",EDGE,"E37")}),1.0]])]});
            extrude(context, id + "F13", {"entities" : qUnion([Q0]), "operationType" : NewBodyOperationType.REMOVE, "depth" : 1 * mm, "offsetDistance" : 25 * mm});
        }
    });
